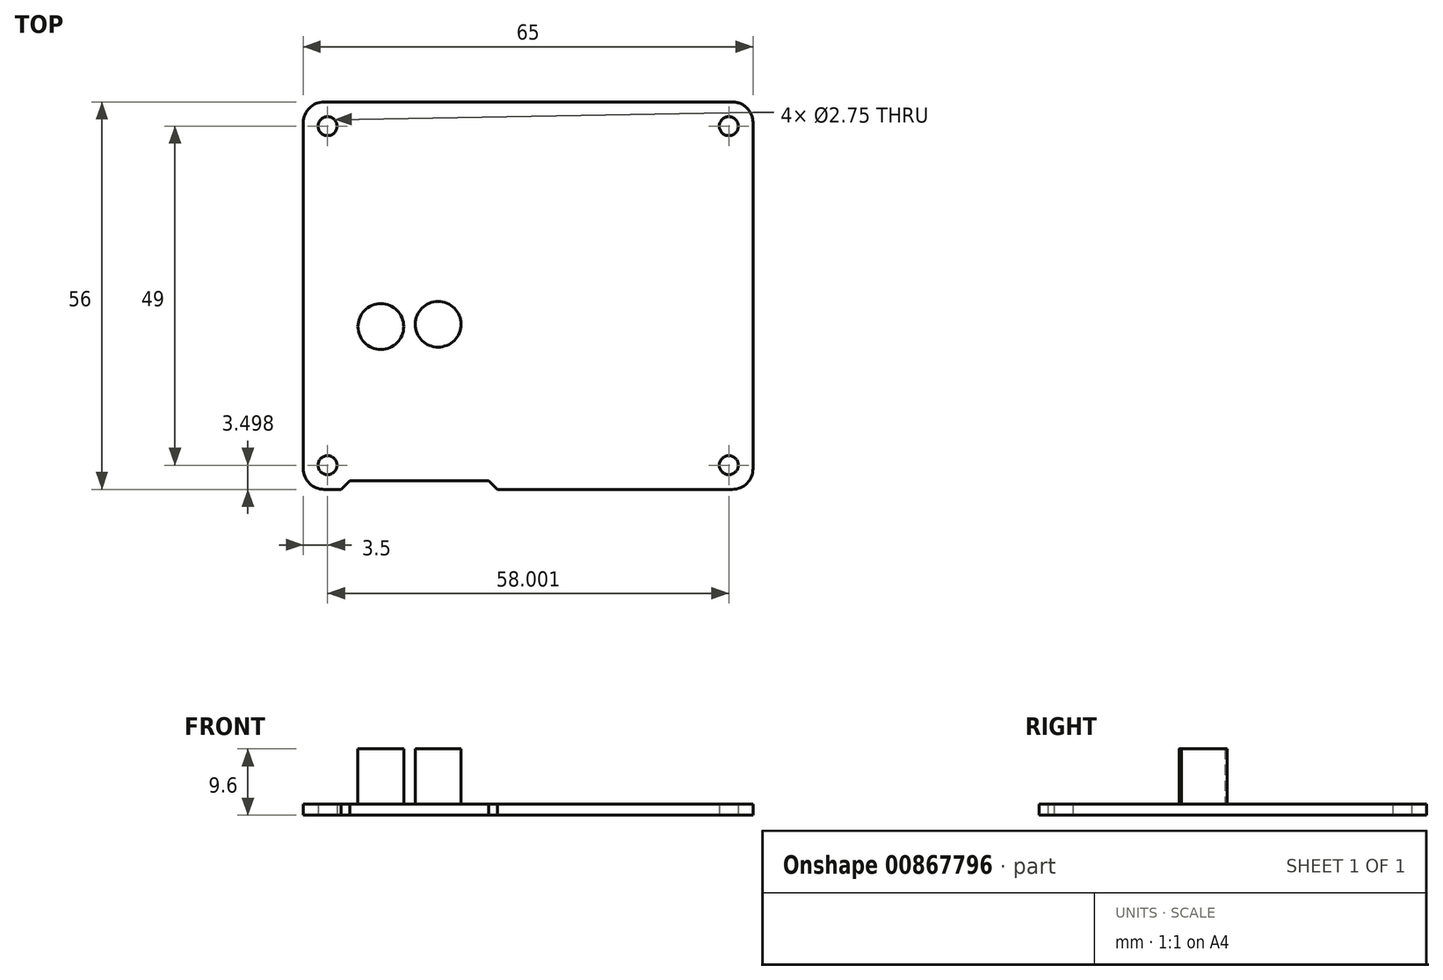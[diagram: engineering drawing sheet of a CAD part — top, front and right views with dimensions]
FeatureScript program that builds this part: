
annotation { "Feature Type Name" : "Feature", "Feature Type Description" : "" }
export const myFeature = defineFeature(function(context is Context, id is Id, definition is map)
    precondition{}
    {
        {
            var Q0;
            Q0=qCreatedBy(makeId("Top.planeOp"),FACE);
            var sketch = newSketch(context, id + "F0", { "sketchPlane" : qUnion([Q0])});
            skArc(sketch, "E0", {"start": v(-30.1, -23.27) * mm, "mid": v(-29.22, -25.4) * mm, "end": v(-27.1, -26.27) * mm});
            skArc(sketch, "E1", {"start": v(31.9, -26.27) * mm, "mid": v(34.02, -25.4) * mm, "end": v(34.9, -23.27) * mm});
            skArc(sketch, "E2", {"start": v(-27.1, 29.73) * mm, "mid": v(-29.22, 28.85) * mm, "end": v(-30.1, 26.73) * mm});
            skArc(sketch, "E3", {"start": v(34.9, 26.73) * mm, "mid": v(34.02, 28.85) * mm, "end": v(31.9, 29.73) * mm});
            skLineSegment(sketch, "E4", {"start": v(-23.37, -25) * mm, "end": v(-3.3, -25) * mm});
            skLineSegment(sketch, "E5", {"start": v(-24.64, -26.27) * mm, "end": v(-23.37, -25) * mm});
            skLineSegment(sketch, "E6", {"start": v(-2.03, -26.27) * mm, "end": v(31.9, -26.27) * mm});
            skLineSegment(sketch, "E7", {"start": v(-27.1, 29.73) * mm, "end": v(31.9, 29.73) * mm});
            skLineSegment(sketch, "E8", {"start": v(-3.3, -25) * mm, "end": v(-2.03, -26.27) * mm});
            skLineSegment(sketch, "E9", {"start": v(-30.1, -23.27) * mm, "end": v(-30.1, 26.73) * mm});
            skLineSegment(sketch, "E10", {"start": v(34.9, -23.27) * mm, "end": v(34.9, 26.73) * mm});
            skLineSegment(sketch, "E11", {"start": v(-27.97, 26.23) * mm, "end": v(-25.23, 26.23) * mm});
            skLineSegment(sketch, "E12", {"start": v(-26.6, 24.85) * mm, "end": v(-26.6, 27.6) * mm});
            skLineSegment(sketch, "E13", {"start": v(30.02, 26.23) * mm, "end": v(32.77, 26.23) * mm});
            skLineSegment(sketch, "E14", {"start": v(31.4, 24.85) * mm, "end": v(31.4, 27.6) * mm});
            skLineSegment(sketch, "E15", {"start": v(30.02, -22.77) * mm, "end": v(32.77, -22.77) * mm});
            skLineSegment(sketch, "E16", {"start": v(31.4, -24.15) * mm, "end": v(31.4, -21.4) * mm});
            skLineSegment(sketch, "E17", {"start": v(-27.97, -22.77) * mm, "end": v(-25.23, -22.77) * mm});
            skLineSegment(sketch, "E18", {"start": v(-26.6, -24.15) * mm, "end": v(-26.6, -21.4) * mm});
            skLineSegment(sketch, "E19", {"start": v(5.2, -13.06) * mm, "end": v(6.22, -13.06) * mm});
            skLineSegment(sketch, "E20", {"start": v(5.71, -13.57) * mm, "end": v(5.71, -12.56) * mm});
            skLineSegment(sketch, "E21", {"start": v(7.75, -13.06) * mm, "end": v(8.76, -13.06) * mm});
            skLineSegment(sketch, "E22", {"start": v(8.25, -13.57) * mm, "end": v(8.25, -12.56) * mm});
            skLineSegment(sketch, "E23", {"start": v(10.29, -13.06) * mm, "end": v(11.3, -13.06) * mm});
            skLineSegment(sketch, "E24", {"start": v(10.8, -13.57) * mm, "end": v(10.8, -12.56) * mm});
            skLineSegment(sketch, "E25", {"start": v(22.99, -13.06) * mm, "end": v(24, -13.06) * mm});
            skLineSegment(sketch, "E26", {"start": v(23.5, -13.57) * mm, "end": v(23.5, -12.56) * mm});
            skLineSegment(sketch, "E27", {"start": v(25.53, -13.06) * mm, "end": v(26.54, -13.06) * mm});
            skLineSegment(sketch, "E28", {"start": v(26.03, -13.57) * mm, "end": v(26.03, -12.56) * mm});
            skLineSegment(sketch, "E29", {"start": v(28.07, -13.06) * mm, "end": v(29.08, -13.06) * mm});
            skLineSegment(sketch, "E30", {"start": v(28.57, -13.57) * mm, "end": v(28.57, -12.56) * mm});
            skLineSegment(sketch, "E31", {"start": v(30.6, -13.06) * mm, "end": v(31.62, -13.06) * mm});
            skLineSegment(sketch, "E32", {"start": v(31.11, -13.57) * mm, "end": v(31.11, -12.56) * mm});
            skLineSegment(sketch, "E33", {"start": v(33.15, -13.06) * mm, "end": v(34.16, -13.06) * mm});
            skLineSegment(sketch, "E34", {"start": v(33.65, -13.57) * mm, "end": v(33.65, -12.56) * mm});
            skLineSegment(sketch, "E35", {"start": v(20.45, -13.06) * mm, "end": v(21.46, -13.06) * mm});
            skLineSegment(sketch, "E36", {"start": v(20.95, -13.57) * mm, "end": v(20.95, -12.56) * mm});
            skLineSegment(sketch, "E37", {"start": v(17.9, -13.06) * mm, "end": v(18.92, -13.06) * mm});
            skLineSegment(sketch, "E38", {"start": v(18.41, -13.57) * mm, "end": v(18.41, -12.56) * mm});
            skLineSegment(sketch, "E39", {"start": v(15.37, -13.06) * mm, "end": v(16.38, -13.06) * mm});
            skLineSegment(sketch, "E40", {"start": v(15.87, -13.57) * mm, "end": v(15.87, -12.56) * mm});
            skLineSegment(sketch, "E41", {"start": v(12.83, -13.06) * mm, "end": v(13.84, -13.06) * mm});
            skLineSegment(sketch, "E42", {"start": v(13.33, -13.57) * mm, "end": v(13.33, -12.56) * mm});
            skLineSegment(sketch, "E43", {"start": v(2.67, -13.06) * mm, "end": v(3.68, -13.06) * mm});
            skLineSegment(sketch, "E44", {"start": v(3.17, -13.57) * mm, "end": v(3.17, -12.56) * mm});
            skLineSegment(sketch, "E45", {"start": v(0.13, -13.06) * mm, "end": v(1.14, -13.06) * mm});
            skLineSegment(sketch, "E46", {"start": v(0.63, -13.57) * mm, "end": v(0.63, -12.56) * mm});
            skLineSegment(sketch, "E47", {"start": v(-2.29, -7.35) * mm, "end": v(-1.27, -7.35) * mm});
            skLineSegment(sketch, "E48", {"start": v(-1.78, -7.86) * mm, "end": v(-1.78, -6.84) * mm});
            skLineSegment(sketch, "E49", {"start": v(-2.29, -4.8) * mm, "end": v(-1.27, -4.8) * mm});
            skLineSegment(sketch, "E50", {"start": v(-1.78, -5.32) * mm, "end": v(-1.78, -4.3) * mm});
            skLineSegment(sketch, "E51", {"start": v(0.25, -7.35) * mm, "end": v(1.27, -7.35) * mm});
            skLineSegment(sketch, "E52", {"start": v(0.76, -7.86) * mm, "end": v(0.76, -6.84) * mm});
            skLineSegment(sketch, "E53", {"start": v(0.25, -4.8) * mm, "end": v(1.27, -4.8) * mm});
            skLineSegment(sketch, "E54", {"start": v(0.76, -5.32) * mm, "end": v(0.76, -4.3) * mm});
            skLineSegment(sketch, "E55", {"start": v(2.8, -7.35) * mm, "end": v(3.8, -7.35) * mm});
            skLineSegment(sketch, "E56", {"start": v(3.3, -7.86) * mm, "end": v(3.3, -6.84) * mm});
            skLineSegment(sketch, "E57", {"start": v(2.8, -4.8) * mm, "end": v(3.8, -4.8) * mm});
            skLineSegment(sketch, "E58", {"start": v(3.3, -5.32) * mm, "end": v(3.3, -4.3) * mm});
            skLineSegment(sketch, "E59", {"start": v(-15.88, 16.15) * mm, "end": v(-14.86, 16.15) * mm});
            skLineSegment(sketch, "E60", {"start": v(-15.37, 15.64) * mm, "end": v(-15.37, 16.65) * mm});
            skLineSegment(sketch, "E61", {"start": v(-18.42, 16.15) * mm, "end": v(-17.4, 16.15) * mm});
            skLineSegment(sketch, "E62", {"start": v(-17.9, 15.64) * mm, "end": v(-17.9, 16.65) * mm});
            skLineSegment(sketch, "E63", {"start": v(-18.42, 13.6) * mm, "end": v(-17.4, 13.6) * mm});
            skLineSegment(sketch, "E64", {"start": v(-17.9, 13.1) * mm, "end": v(-17.9, 14.11) * mm});
            skLineSegment(sketch, "E65", {"start": v(26.02, 27.5) * mm, "end": v(27.04, 27.5) * mm});
            skLineSegment(sketch, "E66", {"start": v(26.53, 26.99) * mm, "end": v(26.53, 28) * mm});
            skLineSegment(sketch, "E67", {"start": v(26.02, 24.96) * mm, "end": v(27.04, 24.96) * mm});
            skLineSegment(sketch, "E68", {"start": v(26.53, 24.45) * mm, "end": v(26.53, 25.46) * mm});
            skLineSegment(sketch, "E69", {"start": v(23.48, 27.5) * mm, "end": v(24.5, 27.5) * mm});
            skLineSegment(sketch, "E70", {"start": v(23.99, 26.99) * mm, "end": v(23.99, 28) * mm});
            skLineSegment(sketch, "E71", {"start": v(23.48, 24.96) * mm, "end": v(24.5, 24.96) * mm});
            skLineSegment(sketch, "E72", {"start": v(23.99, 24.45) * mm, "end": v(23.99, 25.46) * mm});
            skLineSegment(sketch, "E73", {"start": v(20.94, 27.5) * mm, "end": v(21.96, 27.5) * mm});
            skLineSegment(sketch, "E74", {"start": v(21.45, 26.99) * mm, "end": v(21.45, 28) * mm});
            skLineSegment(sketch, "E75", {"start": v(20.94, 24.96) * mm, "end": v(21.96, 24.96) * mm});
            skLineSegment(sketch, "E76", {"start": v(21.45, 24.45) * mm, "end": v(21.45, 25.46) * mm});
            skLineSegment(sketch, "E77", {"start": v(18.4, 27.5) * mm, "end": v(19.42, 27.5) * mm});
            skLineSegment(sketch, "E78", {"start": v(18.9, 26.99) * mm, "end": v(18.9, 28) * mm});
            skLineSegment(sketch, "E79", {"start": v(18.4, 24.96) * mm, "end": v(19.42, 24.96) * mm});
            skLineSegment(sketch, "E80", {"start": v(18.9, 24.45) * mm, "end": v(18.9, 25.46) * mm});
            skLineSegment(sketch, "E81", {"start": v(15.86, 27.5) * mm, "end": v(16.88, 27.5) * mm});
            skLineSegment(sketch, "E82", {"start": v(16.37, 26.99) * mm, "end": v(16.37, 28) * mm});
            skLineSegment(sketch, "E83", {"start": v(15.86, 24.96) * mm, "end": v(16.88, 24.96) * mm});
            skLineSegment(sketch, "E84", {"start": v(16.37, 24.45) * mm, "end": v(16.37, 25.46) * mm});
            skLineSegment(sketch, "E85", {"start": v(13.32, 27.5) * mm, "end": v(14.34, 27.5) * mm});
            skLineSegment(sketch, "E86", {"start": v(13.83, 26.99) * mm, "end": v(13.83, 28) * mm});
            skLineSegment(sketch, "E87", {"start": v(13.32, 24.96) * mm, "end": v(14.34, 24.96) * mm});
            skLineSegment(sketch, "E88", {"start": v(13.83, 24.45) * mm, "end": v(13.83, 25.46) * mm});
            skLineSegment(sketch, "E89", {"start": v(10.78, 27.5) * mm, "end": v(11.8, 27.5) * mm});
            skLineSegment(sketch, "E90", {"start": v(11.29, 26.99) * mm, "end": v(11.29, 28) * mm});
            skLineSegment(sketch, "E91", {"start": v(10.78, 24.96) * mm, "end": v(11.8, 24.96) * mm});
            skLineSegment(sketch, "E92", {"start": v(11.29, 24.45) * mm, "end": v(11.29, 25.46) * mm});
            skLineSegment(sketch, "E93", {"start": v(8.24, 27.5) * mm, "end": v(9.26, 27.5) * mm});
            skLineSegment(sketch, "E94", {"start": v(8.75, 26.99) * mm, "end": v(8.75, 28) * mm});
            skLineSegment(sketch, "E95", {"start": v(8.24, 24.96) * mm, "end": v(9.26, 24.96) * mm});
            skLineSegment(sketch, "E96", {"start": v(8.75, 24.45) * mm, "end": v(8.75, 25.46) * mm});
            skLineSegment(sketch, "E97", {"start": v(5.7, 27.5) * mm, "end": v(6.72, 27.5) * mm});
            skLineSegment(sketch, "E98", {"start": v(6.2, 26.99) * mm, "end": v(6.2, 28) * mm});
            skLineSegment(sketch, "E99", {"start": v(5.7, 24.96) * mm, "end": v(6.72, 24.96) * mm});
            skLineSegment(sketch, "E100", {"start": v(6.2, 24.45) * mm, "end": v(6.2, 25.46) * mm});
            skLineSegment(sketch, "E101", {"start": v(3.16, 27.5) * mm, "end": v(4.18, 27.5) * mm});
            skLineSegment(sketch, "E102", {"start": v(3.67, 26.99) * mm, "end": v(3.67, 28) * mm});
            skLineSegment(sketch, "E103", {"start": v(3.16, 24.96) * mm, "end": v(4.18, 24.96) * mm});
            skLineSegment(sketch, "E104", {"start": v(3.67, 24.45) * mm, "end": v(3.67, 25.46) * mm});
            skLineSegment(sketch, "E105", {"start": v(0.62, 27.5) * mm, "end": v(1.64, 27.5) * mm});
            skLineSegment(sketch, "E106", {"start": v(1.13, 26.99) * mm, "end": v(1.13, 28) * mm});
            skLineSegment(sketch, "E107", {"start": v(0.62, 24.96) * mm, "end": v(1.64, 24.96) * mm});
            skLineSegment(sketch, "E108", {"start": v(1.13, 24.45) * mm, "end": v(1.13, 25.46) * mm});
            skLineSegment(sketch, "E109", {"start": v(-1.92, 27.5) * mm, "end": v(-0.9, 27.5) * mm});
            skLineSegment(sketch, "E110", {"start": v(-1.41, 26.99) * mm, "end": v(-1.41, 28) * mm});
            skLineSegment(sketch, "E111", {"start": v(-1.92, 24.96) * mm, "end": v(-0.9, 24.96) * mm});
            skLineSegment(sketch, "E112", {"start": v(-1.41, 24.45) * mm, "end": v(-1.41, 25.46) * mm});
            skLineSegment(sketch, "E113", {"start": v(-4.46, 27.5) * mm, "end": v(-3.44, 27.5) * mm});
            skLineSegment(sketch, "E114", {"start": v(-3.95, 26.99) * mm, "end": v(-3.95, 28) * mm});
            skLineSegment(sketch, "E115", {"start": v(-4.46, 24.96) * mm, "end": v(-3.44, 24.96) * mm});
            skLineSegment(sketch, "E116", {"start": v(-3.95, 24.45) * mm, "end": v(-3.95, 25.46) * mm});
            skLineSegment(sketch, "E117", {"start": v(-7, 27.5) * mm, "end": v(-5.98, 27.5) * mm});
            skLineSegment(sketch, "E118", {"start": v(-6.5, 26.99) * mm, "end": v(-6.5, 28) * mm});
            skLineSegment(sketch, "E119", {"start": v(-7, 24.96) * mm, "end": v(-5.98, 24.96) * mm});
            skLineSegment(sketch, "E120", {"start": v(-6.5, 24.45) * mm, "end": v(-6.5, 25.46) * mm});
            skLineSegment(sketch, "E121", {"start": v(-9.54, 27.5) * mm, "end": v(-8.52, 27.5) * mm});
            skLineSegment(sketch, "E122", {"start": v(-9.03, 26.99) * mm, "end": v(-9.03, 28) * mm});
            skLineSegment(sketch, "E123", {"start": v(-9.54, 24.96) * mm, "end": v(-8.52, 24.96) * mm});
            skLineSegment(sketch, "E124", {"start": v(-9.03, 24.45) * mm, "end": v(-9.03, 25.46) * mm});
            skLineSegment(sketch, "E125", {"start": v(-12.08, 27.5) * mm, "end": v(-11.06, 27.5) * mm});
            skLineSegment(sketch, "E126", {"start": v(-11.57, 26.99) * mm, "end": v(-11.57, 28) * mm});
            skLineSegment(sketch, "E127", {"start": v(-12.08, 24.96) * mm, "end": v(-11.06, 24.96) * mm});
            skLineSegment(sketch, "E128", {"start": v(-11.57, 24.45) * mm, "end": v(-11.57, 25.46) * mm});
            skLineSegment(sketch, "E129", {"start": v(-14.62, 27.5) * mm, "end": v(-13.6, 27.5) * mm});
            skLineSegment(sketch, "E130", {"start": v(-14.11, 26.99) * mm, "end": v(-14.11, 28) * mm});
            skLineSegment(sketch, "E131", {"start": v(-14.62, 24.96) * mm, "end": v(-13.6, 24.96) * mm});
            skLineSegment(sketch, "E132", {"start": v(-14.11, 24.45) * mm, "end": v(-14.11, 25.46) * mm});
            skLineSegment(sketch, "E133", {"start": v(-17.16, 27.5) * mm, "end": v(-16.14, 27.5) * mm});
            skLineSegment(sketch, "E134", {"start": v(-16.65, 26.99) * mm, "end": v(-16.65, 28) * mm});
            skLineSegment(sketch, "E135", {"start": v(-17.16, 24.96) * mm, "end": v(-16.14, 24.96) * mm});
            skLineSegment(sketch, "E136", {"start": v(-16.65, 24.45) * mm, "end": v(-16.65, 25.46) * mm});
            skLineSegment(sketch, "E137", {"start": v(-19.7, 27.5) * mm, "end": v(-18.68, 27.5) * mm});
            skLineSegment(sketch, "E138", {"start": v(-19.2, 26.99) * mm, "end": v(-19.2, 28) * mm});
            skLineSegment(sketch, "E139", {"start": v(-19.7, 24.96) * mm, "end": v(-18.68, 24.96) * mm});
            skLineSegment(sketch, "E140", {"start": v(-19.2, 24.45) * mm, "end": v(-19.2, 25.46) * mm});
            skLineSegment(sketch, "E141", {"start": v(-22.24, 27.5) * mm, "end": v(-21.22, 27.5) * mm});
            skLineSegment(sketch, "E142", {"start": v(-21.73, 26.99) * mm, "end": v(-21.73, 28) * mm});
            skLineSegment(sketch, "E143", {"start": v(-22.24, 24.96) * mm, "end": v(-21.22, 24.96) * mm});
            skLineSegment(sketch, "E144", {"start": v(-21.73, 24.45) * mm, "end": v(-21.73, 25.46) * mm});
            skLineSegment(sketch, "E145", {"start": v(-8.1, -23.1) * mm, "end": v(-7.2, -23.1) * mm});
            skLineSegment(sketch, "E146", {"start": v(-7.64, -23.55) * mm, "end": v(-7.64, -22.65) * mm});
            skLineSegment(sketch, "E147", {"start": v(-11.1, -23.1) * mm, "end": v(-10.2, -23.1) * mm});
            skLineSegment(sketch, "E148", {"start": v(-10.65, -23.55) * mm, "end": v(-10.65, -22.65) * mm});
            skLineSegment(sketch, "E149", {"start": v(-7.11, -19.29) * mm, "end": v(-6.1, -19.29) * mm});
            skLineSegment(sketch, "E150", {"start": v(-6.6, -19.8) * mm, "end": v(-6.6, -18.78) * mm});
            skLineSegment(sketch, "E151", {"start": v(-9.65, -19.29) * mm, "end": v(-8.64, -19.29) * mm});
            skLineSegment(sketch, "E152", {"start": v(-9.15, -19.8) * mm, "end": v(-9.15, -18.78) * mm});
            skLineSegment(sketch, "E153", {"start": v(-12.2, -19.29) * mm, "end": v(-11.18, -19.29) * mm});
            skLineSegment(sketch, "E154", {"start": v(-11.69, -19.8) * mm, "end": v(-11.69, -18.78) * mm});
            skLineSegment(sketch, "E155", {"start": v(1.29, -24.11) * mm, "end": v(1.99, -24.11) * mm});
            skLineSegment(sketch, "E156", {"start": v(1.64, -24.46) * mm, "end": v(1.64, -23.76) * mm});
            skLineSegment(sketch, "E157", {"start": v(3.09, -24.11) * mm, "end": v(3.79, -24.11) * mm});
            skLineSegment(sketch, "E158", {"start": v(3.44, -24.46) * mm, "end": v(3.44, -23.76) * mm});
            skLineSegment(sketch, "E159", {"start": v(25.95, -24.11) * mm, "end": v(26.65, -24.11) * mm});
            skLineSegment(sketch, "E160", {"start": v(26.3, -24.46) * mm, "end": v(26.3, -23.76) * mm});
            skLineSegment(sketch, "E161", {"start": v(24.15, -24.11) * mm, "end": v(24.85, -24.11) * mm});
            skLineSegment(sketch, "E162", {"start": v(24.5, -24.46) * mm, "end": v(24.5, -23.76) * mm});
            skLineSegment(sketch, "E163", {"start": v(12.72, -24.11) * mm, "end": v(13.42, -24.11) * mm});
            skLineSegment(sketch, "E164", {"start": v(13.07, -24.46) * mm, "end": v(13.07, -23.76) * mm});
            skLineSegment(sketch, "E165", {"start": v(14.52, -24.11) * mm, "end": v(15.22, -24.11) * mm});
            skLineSegment(sketch, "E166", {"start": v(14.87, -24.46) * mm, "end": v(14.87, -23.76) * mm});
            skLineSegment(sketch, "E167", {"start": v(32.41, 15.14) * mm, "end": v(33.12, 15.14) * mm});
            skLineSegment(sketch, "E168", {"start": v(32.76, 14.8) * mm, "end": v(32.76, 15.5) * mm});
            skLineSegment(sketch, "E169", {"start": v(32.41, 13.34) * mm, "end": v(33.12, 13.34) * mm});
            skLineSegment(sketch, "E170", {"start": v(32.76, 13) * mm, "end": v(32.76, 13.69) * mm});
            skLineSegment(sketch, "E171", {"start": v(22.99, 7.26) * mm, "end": v(24, 7.26) * mm});
            skLineSegment(sketch, "E172", {"start": v(23.5, 6.75) * mm, "end": v(23.5, 7.76) * mm});
            skLineSegment(sketch, "E173", {"start": v(25.53, 7.26) * mm, "end": v(26.54, 7.26) * mm});
            skLineSegment(sketch, "E174", {"start": v(26.03, 6.75) * mm, "end": v(26.03, 7.76) * mm});
            skLineSegment(sketch, "E175", {"start": v(28.07, 7.26) * mm, "end": v(29.08, 7.26) * mm});
            skLineSegment(sketch, "E176", {"start": v(28.57, 6.75) * mm, "end": v(28.57, 7.76) * mm});
            skLineSegment(sketch, "E177", {"start": v(30.6, 7.26) * mm, "end": v(31.62, 7.26) * mm});
            skLineSegment(sketch, "E178", {"start": v(31.11, 6.75) * mm, "end": v(31.11, 7.76) * mm});
            skLineSegment(sketch, "E179", {"start": v(33.15, 7.26) * mm, "end": v(34.16, 7.26) * mm});
            skLineSegment(sketch, "E180", {"start": v(33.65, 6.75) * mm, "end": v(33.65, 7.76) * mm});
            skLineSegment(sketch, "E181", {"start": v(20.45, 7.26) * mm, "end": v(21.46, 7.26) * mm});
            skLineSegment(sketch, "E182", {"start": v(20.95, 6.75) * mm, "end": v(20.95, 7.76) * mm});
            skLineSegment(sketch, "E183", {"start": v(17.9, 7.26) * mm, "end": v(18.92, 7.26) * mm});
            skLineSegment(sketch, "E184", {"start": v(18.41, 6.75) * mm, "end": v(18.41, 7.76) * mm});
            skLineSegment(sketch, "E185", {"start": v(15.37, 7.26) * mm, "end": v(16.38, 7.26) * mm});
            skLineSegment(sketch, "E186", {"start": v(15.87, 6.75) * mm, "end": v(15.87, 7.76) * mm});
            skLineSegment(sketch, "E187", {"start": v(0.13, 4.72) * mm, "end": v(1.14, 4.72) * mm});
            skLineSegment(sketch, "E188", {"start": v(0.63, 4.2) * mm, "end": v(0.63, 5.22) * mm});
            skLineSegment(sketch, "E189", {"start": v(2.67, 4.72) * mm, "end": v(3.68, 4.72) * mm});
            skLineSegment(sketch, "E190", {"start": v(3.17, 4.2) * mm, "end": v(3.17, 5.22) * mm});
            skLineSegment(sketch, "E191", {"start": v(12.83, 4.72) * mm, "end": v(13.84, 4.72) * mm});
            skLineSegment(sketch, "E192", {"start": v(13.33, 4.2) * mm, "end": v(13.33, 5.22) * mm});
            skLineSegment(sketch, "E193", {"start": v(15.37, 4.72) * mm, "end": v(16.38, 4.72) * mm});
            skLineSegment(sketch, "E194", {"start": v(15.87, 4.2) * mm, "end": v(15.87, 5.22) * mm});
            skLineSegment(sketch, "E195", {"start": v(17.9, 4.72) * mm, "end": v(18.92, 4.72) * mm});
            skLineSegment(sketch, "E196", {"start": v(18.41, 4.2) * mm, "end": v(18.41, 5.22) * mm});
            skLineSegment(sketch, "E197", {"start": v(20.45, 4.72) * mm, "end": v(21.46, 4.72) * mm});
            skLineSegment(sketch, "E198", {"start": v(20.95, 4.2) * mm, "end": v(20.95, 5.22) * mm});
            skLineSegment(sketch, "E199", {"start": v(33.15, 4.72) * mm, "end": v(34.16, 4.72) * mm});
            skLineSegment(sketch, "E200", {"start": v(33.65, 4.2) * mm, "end": v(33.65, 5.22) * mm});
            skLineSegment(sketch, "E201", {"start": v(30.6, 4.72) * mm, "end": v(31.62, 4.72) * mm});
            skLineSegment(sketch, "E202", {"start": v(31.11, 4.2) * mm, "end": v(31.11, 5.22) * mm});
            skLineSegment(sketch, "E203", {"start": v(28.07, 4.72) * mm, "end": v(29.08, 4.72) * mm});
            skLineSegment(sketch, "E204", {"start": v(28.57, 4.2) * mm, "end": v(28.57, 5.22) * mm});
            skLineSegment(sketch, "E205", {"start": v(25.53, 4.72) * mm, "end": v(26.54, 4.72) * mm});
            skLineSegment(sketch, "E206", {"start": v(26.03, 4.2) * mm, "end": v(26.03, 5.22) * mm});
            skLineSegment(sketch, "E207", {"start": v(22.99, 4.72) * mm, "end": v(24, 4.72) * mm});
            skLineSegment(sketch, "E208", {"start": v(23.5, 4.2) * mm, "end": v(23.5, 5.22) * mm});
            skLineSegment(sketch, "E209", {"start": v(10.29, 4.72) * mm, "end": v(11.3, 4.72) * mm});
            skLineSegment(sketch, "E210", {"start": v(10.8, 4.2) * mm, "end": v(10.8, 5.22) * mm});
            skLineSegment(sketch, "E211", {"start": v(7.75, 4.72) * mm, "end": v(8.76, 4.72) * mm});
            skLineSegment(sketch, "E212", {"start": v(8.25, 4.2) * mm, "end": v(8.25, 5.22) * mm});
            skLineSegment(sketch, "E213", {"start": v(5.2, 4.72) * mm, "end": v(6.22, 4.72) * mm});
            skLineSegment(sketch, "E214", {"start": v(5.71, 4.2) * mm, "end": v(5.71, 5.22) * mm});
            skLineSegment(sketch, "E215", {"start": v(-5.59, 1.29) * mm, "end": v(-4.57, 1.29) * mm});
            skLineSegment(sketch, "E216", {"start": v(-5.08, 0.78) * mm, "end": v(-5.08, 1.8) * mm});
            skLineSegment(sketch, "E217", {"start": v(-3.05, 1.29) * mm, "end": v(-2.03, 1.29) * mm});
            skLineSegment(sketch, "E218", {"start": v(-2.54, 0.78) * mm, "end": v(-2.54, 1.8) * mm});
            skLineSegment(sketch, "E219", {"start": v(1.01, -0.87) * mm, "end": v(2.03, -0.87) * mm});
            skLineSegment(sketch, "E220", {"start": v(1.52, -1.38) * mm, "end": v(1.52, -0.36) * mm});
            skLineSegment(sketch, "E221", {"start": v(3.55, -0.87) * mm, "end": v(4.57, -0.87) * mm});
            skLineSegment(sketch, "E222", {"start": v(4.06, -1.38) * mm, "end": v(4.06, -0.36) * mm});
            skLineSegment(sketch, "E223", {"start": v(-16.95, -20.68) * mm, "end": v(-16.4, -20.68) * mm});
            skLineSegment(sketch, "E224", {"start": v(-16.68, -20.96) * mm, "end": v(-16.68, -20.41) * mm});
            skLineSegment(sketch, "E225", {"start": v(-22.95, -23.38) * mm, "end": v(-22.4, -23.38) * mm});
            skLineSegment(sketch, "E226", {"start": v(-22.68, -23.66) * mm, "end": v(-22.68, -23.11) * mm});
            skLineSegment(sketch, "E227", {"start": v(-21.95, -20.68) * mm, "end": v(-21.4, -20.68) * mm});
            skLineSegment(sketch, "E228", {"start": v(-21.68, -20.96) * mm, "end": v(-21.68, -20.41) * mm});
            skLineSegment(sketch, "E229", {"start": v(-15.95, -23.38) * mm, "end": v(-15.4, -23.38) * mm});
            skLineSegment(sketch, "E230", {"start": v(-15.68, -23.66) * mm, "end": v(-15.68, -23.11) * mm});
            skLineSegment(sketch, "E231", {"start": v(-6.41, 7.13) * mm, "end": v(-5.53, 7.13) * mm});
            skLineSegment(sketch, "E232", {"start": v(-5.97, 6.68) * mm, "end": v(-5.97, 7.57) * mm});
            skLineSegment(sketch, "E233", {"start": v(-6.41, 10.88) * mm, "end": v(-5.53, 10.88) * mm});
            skLineSegment(sketch, "E234", {"start": v(-5.97, 10.43) * mm, "end": v(-5.97, 11.32) * mm});
            skLineSegment(sketch, "E235", {"start": v(-20.14, -17.26) * mm, "end": v(-19.14, -17.26) * mm});
            skLineSegment(sketch, "E236", {"start": v(-19.64, -17.76) * mm, "end": v(-19.64, -16.76) * mm});
            skLineSegment(sketch, "E237", {"start": v(-23.14, -12.56) * mm, "end": v(-22.14, -12.56) * mm});
            skLineSegment(sketch, "E238", {"start": v(-22.64, -13.06) * mm, "end": v(-22.64, -12.06) * mm});
            skLineSegment(sketch, "E239", {"start": v(-17.14, -12.56) * mm, "end": v(-16.14, -12.56) * mm});
            skLineSegment(sketch, "E240", {"start": v(-16.64, -13.06) * mm, "end": v(-16.64, -12.06) * mm});
            skLineSegment(sketch, "E241", {"start": v(-27.05, 11.94) * mm, "end": v(-25.53, 11.94) * mm});
            skLineSegment(sketch, "E242", {"start": v(-26.3, 11.18) * mm, "end": v(-26.3, 12.7) * mm});
            skLineSegment(sketch, "E243", {"start": v(-27.05, 8.44) * mm, "end": v(-25.53, 8.44) * mm});
            skLineSegment(sketch, "E244", {"start": v(-26.3, 7.68) * mm, "end": v(-26.3, 9.2) * mm});
            skLineSegment(sketch, "E245", {"start": v(-27.05, 4.94) * mm, "end": v(-25.53, 4.94) * mm});
            skLineSegment(sketch, "E246", {"start": v(-26.3, 4.18) * mm, "end": v(-26.3, 5.7) * mm});
            skLineSegment(sketch, "E247", {"start": v(-27.05, 1.44) * mm, "end": v(-25.53, 1.44) * mm});
            skLineSegment(sketch, "E248", {"start": v(-26.3, 0.68) * mm, "end": v(-26.3, 2.2) * mm});
            skLineSegment(sketch, "E249", {"start": v(-27.05, -2.06) * mm, "end": v(-25.53, -2.06) * mm});
            skLineSegment(sketch, "E250", {"start": v(-26.3, -2.82) * mm, "end": v(-26.3, -1.3) * mm});
            skLineSegment(sketch, "E251", {"start": v(-27.05, -5.56) * mm, "end": v(-25.53, -5.56) * mm});
            skLineSegment(sketch, "E252", {"start": v(-26.3, -6.32) * mm, "end": v(-26.3, -4.8) * mm});
            skLineSegment(sketch, "E253", {"start": v(-27.05, -9.06) * mm, "end": v(-25.53, -9.06) * mm});
            skLineSegment(sketch, "E254", {"start": v(-26.3, -9.82) * mm, "end": v(-26.3, -8.3) * mm});
            skLineSegment(sketch, "E255", {"start": v(-27.05, -12.56) * mm, "end": v(-25.53, -12.56) * mm});
            skLineSegment(sketch, "E256", {"start": v(-26.3, -13.32) * mm, "end": v(-26.3, -11.8) * mm});
            skLineSegment(sketch, "E257", {"start": v(0.13, 7.26) * mm, "end": v(1.14, 7.26) * mm});
            skLineSegment(sketch, "E258", {"start": v(0.63, 6.75) * mm, "end": v(0.63, 7.76) * mm});
            skLineSegment(sketch, "E259", {"start": v(12.83, 7.26) * mm, "end": v(13.84, 7.26) * mm});
            skLineSegment(sketch, "E260", {"start": v(13.33, 6.75) * mm, "end": v(13.33, 7.76) * mm});
            skLineSegment(sketch, "E261", {"start": v(10.29, 7.26) * mm, "end": v(11.3, 7.26) * mm});
            skLineSegment(sketch, "E262", {"start": v(10.8, 6.75) * mm, "end": v(10.8, 7.76) * mm});
            skLineSegment(sketch, "E263", {"start": v(7.75, 7.26) * mm, "end": v(8.76, 7.26) * mm});
            skLineSegment(sketch, "E264", {"start": v(8.25, 6.75) * mm, "end": v(8.25, 7.76) * mm});
            skLineSegment(sketch, "E265", {"start": v(5.2, 7.26) * mm, "end": v(6.22, 7.26) * mm});
            skLineSegment(sketch, "E266", {"start": v(5.71, 6.75) * mm, "end": v(5.71, 7.76) * mm});
            skLineSegment(sketch, "E267", {"start": v(2.67, 7.26) * mm, "end": v(3.68, 7.26) * mm});
            skLineSegment(sketch, "E268", {"start": v(3.17, 6.75) * mm, "end": v(3.17, 7.76) * mm});
            skLineSegment(sketch, "E269", {"start": v(0.13, 9.8) * mm, "end": v(1.14, 9.8) * mm});
            skLineSegment(sketch, "E270", {"start": v(0.63, 9.29) * mm, "end": v(0.63, 10.3) * mm});
            skLineSegment(sketch, "E271", {"start": v(2.67, 9.8) * mm, "end": v(3.68, 9.8) * mm});
            skLineSegment(sketch, "E272", {"start": v(3.17, 9.29) * mm, "end": v(3.17, 10.3) * mm});
            skLineSegment(sketch, "E273", {"start": v(12.83, 9.8) * mm, "end": v(13.84, 9.8) * mm});
            skLineSegment(sketch, "E274", {"start": v(13.33, 9.29) * mm, "end": v(13.33, 10.3) * mm});
            skLineSegment(sketch, "E275", {"start": v(15.37, 9.8) * mm, "end": v(16.38, 9.8) * mm});
            skLineSegment(sketch, "E276", {"start": v(15.87, 9.29) * mm, "end": v(15.87, 10.3) * mm});
            skLineSegment(sketch, "E277", {"start": v(17.9, 9.8) * mm, "end": v(18.92, 9.8) * mm});
            skLineSegment(sketch, "E278", {"start": v(18.41, 9.29) * mm, "end": v(18.41, 10.3) * mm});
            skLineSegment(sketch, "E279", {"start": v(20.45, 9.8) * mm, "end": v(21.46, 9.8) * mm});
            skLineSegment(sketch, "E280", {"start": v(20.95, 9.29) * mm, "end": v(20.95, 10.3) * mm});
            skLineSegment(sketch, "E281", {"start": v(33.15, 9.8) * mm, "end": v(34.16, 9.8) * mm});
            skLineSegment(sketch, "E282", {"start": v(33.65, 9.29) * mm, "end": v(33.65, 10.3) * mm});
            skLineSegment(sketch, "E283", {"start": v(30.6, 9.8) * mm, "end": v(31.62, 9.8) * mm});
            skLineSegment(sketch, "E284", {"start": v(31.11, 9.29) * mm, "end": v(31.11, 10.3) * mm});
            skLineSegment(sketch, "E285", {"start": v(28.07, 9.8) * mm, "end": v(29.08, 9.8) * mm});
            skLineSegment(sketch, "E286", {"start": v(28.57, 9.29) * mm, "end": v(28.57, 10.3) * mm});
            skLineSegment(sketch, "E287", {"start": v(25.53, 9.8) * mm, "end": v(26.54, 9.8) * mm});
            skLineSegment(sketch, "E288", {"start": v(26.03, 9.29) * mm, "end": v(26.03, 10.3) * mm});
            skLineSegment(sketch, "E289", {"start": v(22.99, 9.8) * mm, "end": v(24, 9.8) * mm});
            skLineSegment(sketch, "E290", {"start": v(23.5, 9.29) * mm, "end": v(23.5, 10.3) * mm});
            skLineSegment(sketch, "E291", {"start": v(10.29, 9.8) * mm, "end": v(11.3, 9.8) * mm});
            skLineSegment(sketch, "E292", {"start": v(10.8, 9.29) * mm, "end": v(10.8, 10.3) * mm});
            skLineSegment(sketch, "E293", {"start": v(7.75, 9.8) * mm, "end": v(8.76, 9.8) * mm});
            skLineSegment(sketch, "E294", {"start": v(8.25, 9.29) * mm, "end": v(8.25, 10.3) * mm});
            skLineSegment(sketch, "E295", {"start": v(5.2, 9.8) * mm, "end": v(6.22, 9.8) * mm});
            skLineSegment(sketch, "E296", {"start": v(5.71, 9.29) * mm, "end": v(5.71, 10.3) * mm});
            skLineSegment(sketch, "E297", {"start": v(22.99, -15.6) * mm, "end": v(24, -15.6) * mm});
            skLineSegment(sketch, "E298", {"start": v(23.5, -16.11) * mm, "end": v(23.5, -15.1) * mm});
            skLineSegment(sketch, "E299", {"start": v(25.53, -15.6) * mm, "end": v(26.54, -15.6) * mm});
            skLineSegment(sketch, "E300", {"start": v(26.03, -16.11) * mm, "end": v(26.03, -15.1) * mm});
            skLineSegment(sketch, "E301", {"start": v(28.07, -15.6) * mm, "end": v(29.08, -15.6) * mm});
            skLineSegment(sketch, "E302", {"start": v(28.57, -16.11) * mm, "end": v(28.57, -15.1) * mm});
            skLineSegment(sketch, "E303", {"start": v(30.6, -15.6) * mm, "end": v(31.62, -15.6) * mm});
            skLineSegment(sketch, "E304", {"start": v(31.11, -16.11) * mm, "end": v(31.11, -15.1) * mm});
            skLineSegment(sketch, "E305", {"start": v(33.15, -15.6) * mm, "end": v(34.16, -15.6) * mm});
            skLineSegment(sketch, "E306", {"start": v(33.65, -16.11) * mm, "end": v(33.65, -15.1) * mm});
            skLineSegment(sketch, "E307", {"start": v(20.45, -15.6) * mm, "end": v(21.46, -15.6) * mm});
            skLineSegment(sketch, "E308", {"start": v(20.95, -16.11) * mm, "end": v(20.95, -15.1) * mm});
            skLineSegment(sketch, "E309", {"start": v(0.13, -15.6) * mm, "end": v(1.14, -15.6) * mm});
            skLineSegment(sketch, "E310", {"start": v(0.63, -16.11) * mm, "end": v(0.63, -15.1) * mm});
            skLineSegment(sketch, "E311", {"start": v(2.67, -15.6) * mm, "end": v(3.68, -15.6) * mm});
            skLineSegment(sketch, "E312", {"start": v(3.17, -16.11) * mm, "end": v(3.17, -15.1) * mm});
            skLineSegment(sketch, "E313", {"start": v(5.2, -15.6) * mm, "end": v(6.22, -15.6) * mm});
            skLineSegment(sketch, "E314", {"start": v(5.71, -16.11) * mm, "end": v(5.71, -15.1) * mm});
            skLineSegment(sketch, "E315", {"start": v(17.9, -15.6) * mm, "end": v(18.92, -15.6) * mm});
            skLineSegment(sketch, "E316", {"start": v(18.41, -16.11) * mm, "end": v(18.41, -15.1) * mm});
            skLineSegment(sketch, "E317", {"start": v(15.37, -15.6) * mm, "end": v(16.38, -15.6) * mm});
            skLineSegment(sketch, "E318", {"start": v(15.87, -16.11) * mm, "end": v(15.87, -15.1) * mm});
            skLineSegment(sketch, "E319", {"start": v(12.83, -15.6) * mm, "end": v(13.84, -15.6) * mm});
            skLineSegment(sketch, "E320", {"start": v(13.33, -16.11) * mm, "end": v(13.33, -15.1) * mm});
            skLineSegment(sketch, "E321", {"start": v(10.29, -15.6) * mm, "end": v(11.3, -15.6) * mm});
            skLineSegment(sketch, "E322", {"start": v(10.8, -16.11) * mm, "end": v(10.8, -15.1) * mm});
            skLineSegment(sketch, "E323", {"start": v(7.75, -15.6) * mm, "end": v(8.76, -15.6) * mm});
            skLineSegment(sketch, "E324", {"start": v(8.25, -16.11) * mm, "end": v(8.25, -15.1) * mm});
            skLineSegment(sketch, "E325", {"start": v(0.13, -18.14) * mm, "end": v(1.14, -18.14) * mm});
            skLineSegment(sketch, "E326", {"start": v(0.63, -18.65) * mm, "end": v(0.63, -17.64) * mm});
            skLineSegment(sketch, "E327", {"start": v(2.67, -18.14) * mm, "end": v(3.68, -18.14) * mm});
            skLineSegment(sketch, "E328", {"start": v(3.17, -18.65) * mm, "end": v(3.17, -17.64) * mm});
            skLineSegment(sketch, "E329", {"start": v(12.83, -18.14) * mm, "end": v(13.84, -18.14) * mm});
            skLineSegment(sketch, "E330", {"start": v(13.33, -18.65) * mm, "end": v(13.33, -17.64) * mm});
            skLineSegment(sketch, "E331", {"start": v(15.37, -18.14) * mm, "end": v(16.38, -18.14) * mm});
            skLineSegment(sketch, "E332", {"start": v(15.87, -18.65) * mm, "end": v(15.87, -17.64) * mm});
            skLineSegment(sketch, "E333", {"start": v(17.9, -18.14) * mm, "end": v(18.92, -18.14) * mm});
            skLineSegment(sketch, "E334", {"start": v(18.41, -18.65) * mm, "end": v(18.41, -17.64) * mm});
            skLineSegment(sketch, "E335", {"start": v(20.45, -18.14) * mm, "end": v(21.46, -18.14) * mm});
            skLineSegment(sketch, "E336", {"start": v(20.95, -18.65) * mm, "end": v(20.95, -17.64) * mm});
            skLineSegment(sketch, "E337", {"start": v(33.15, -18.14) * mm, "end": v(34.16, -18.14) * mm});
            skLineSegment(sketch, "E338", {"start": v(33.65, -18.65) * mm, "end": v(33.65, -17.64) * mm});
            skLineSegment(sketch, "E339", {"start": v(30.6, -18.14) * mm, "end": v(31.62, -18.14) * mm});
            skLineSegment(sketch, "E340", {"start": v(31.11, -18.65) * mm, "end": v(31.11, -17.64) * mm});
            skLineSegment(sketch, "E341", {"start": v(28.07, -18.14) * mm, "end": v(29.08, -18.14) * mm});
            skLineSegment(sketch, "E342", {"start": v(28.57, -18.65) * mm, "end": v(28.57, -17.64) * mm});
            skLineSegment(sketch, "E343", {"start": v(25.53, -18.14) * mm, "end": v(26.54, -18.14) * mm});
            skLineSegment(sketch, "E344", {"start": v(26.03, -18.65) * mm, "end": v(26.03, -17.64) * mm});
            skLineSegment(sketch, "E345", {"start": v(22.99, -18.14) * mm, "end": v(24, -18.14) * mm});
            skLineSegment(sketch, "E346", {"start": v(23.5, -18.65) * mm, "end": v(23.5, -17.64) * mm});
            skLineSegment(sketch, "E347", {"start": v(10.29, -18.14) * mm, "end": v(11.3, -18.14) * mm});
            skLineSegment(sketch, "E348", {"start": v(10.8, -18.65) * mm, "end": v(10.8, -17.64) * mm});
            skLineSegment(sketch, "E349", {"start": v(7.75, -18.14) * mm, "end": v(8.76, -18.14) * mm});
            skLineSegment(sketch, "E350", {"start": v(8.25, -18.65) * mm, "end": v(8.25, -17.64) * mm});
            skLineSegment(sketch, "E351", {"start": v(5.2, -18.14) * mm, "end": v(6.22, -18.14) * mm});
            skLineSegment(sketch, "E352", {"start": v(5.71, -18.65) * mm, "end": v(5.71, -17.64) * mm});
            skLineSegment(sketch, "E353", {"start": v(22.22, 21.23) * mm, "end": v(23.24, 21.23) * mm});
            skLineSegment(sketch, "E354", {"start": v(22.73, 20.72) * mm, "end": v(22.73, 21.73) * mm});
            skLineSegment(sketch, "E355", {"start": v(24.76, 21.23) * mm, "end": v(25.78, 21.23) * mm});
            skLineSegment(sketch, "E356", {"start": v(25.27, 20.72) * mm, "end": v(25.27, 21.73) * mm});
            skLineSegment(sketch, "E357", {"start": v(27.3, 21.23) * mm, "end": v(28.32, 21.23) * mm});
            skLineSegment(sketch, "E358", {"start": v(27.81, 20.72) * mm, "end": v(27.81, 21.73) * mm});
            skLineSegment(sketch, "E359", {"start": v(29.84, 21.23) * mm, "end": v(30.86, 21.23) * mm});
            skLineSegment(sketch, "E360", {"start": v(30.35, 20.72) * mm, "end": v(30.35, 21.73) * mm});
            skLineSegment(sketch, "E361", {"start": v(32.38, 21.23) * mm, "end": v(33.4, 21.23) * mm});
            skLineSegment(sketch, "E362", {"start": v(32.9, 20.72) * mm, "end": v(32.9, 21.73) * mm});
            skLineSegment(sketch, "E363", {"start": v(19.68, 21.23) * mm, "end": v(20.7, 21.23) * mm});
            skLineSegment(sketch, "E364", {"start": v(20.2, 20.72) * mm, "end": v(20.2, 21.73) * mm});
            skLineSegment(sketch, "E365", {"start": v(17.14, 21.23) * mm, "end": v(18.16, 21.23) * mm});
            skLineSegment(sketch, "E366", {"start": v(17.65, 20.72) * mm, "end": v(17.65, 21.73) * mm});
            skLineSegment(sketch, "E367", {"start": v(14.6, 21.23) * mm, "end": v(15.62, 21.23) * mm});
            skLineSegment(sketch, "E368", {"start": v(15.11, 20.72) * mm, "end": v(15.11, 21.73) * mm});
            skLineSegment(sketch, "E369", {"start": v(12.06, 21.23) * mm, "end": v(13.08, 21.23) * mm});
            skLineSegment(sketch, "E370", {"start": v(12.57, 20.72) * mm, "end": v(12.57, 21.73) * mm});
            skLineSegment(sketch, "E371", {"start": v(9.52, 21.23) * mm, "end": v(10.54, 21.23) * mm});
            skLineSegment(sketch, "E372", {"start": v(10.03, 20.72) * mm, "end": v(10.03, 21.73) * mm});
            skLineSegment(sketch, "E373", {"start": v(6.98, 21.23) * mm, "end": v(8, 21.23) * mm});
            skLineSegment(sketch, "E374", {"start": v(7.5, 20.72) * mm, "end": v(7.5, 21.73) * mm});
            skLineSegment(sketch, "E375", {"start": v(4.44, 21.23) * mm, "end": v(5.46, 21.23) * mm});
            skLineSegment(sketch, "E376", {"start": v(4.95, 20.72) * mm, "end": v(4.95, 21.73) * mm});
            skLineSegment(sketch, "E377", {"start": v(1.9, 21.23) * mm, "end": v(2.92, 21.23) * mm});
            skLineSegment(sketch, "E378", {"start": v(2.41, 20.72) * mm, "end": v(2.41, 21.73) * mm});
            skLineSegment(sketch, "E379", {"start": v(-8.26, 21.23) * mm, "end": v(-7.24, 21.23) * mm});
            skLineSegment(sketch, "E380", {"start": v(-7.75, 20.72) * mm, "end": v(-7.75, 21.73) * mm});
            skLineSegment(sketch, "E381", {"start": v(-10.8, 21.23) * mm, "end": v(-9.78, 21.23) * mm});
            skLineSegment(sketch, "E382", {"start": v(-10.29, 20.72) * mm, "end": v(-10.29, 21.73) * mm});
            skLineSegment(sketch, "E383", {"start": v(-13.34, 21.23) * mm, "end": v(-12.32, 21.23) * mm});
            skLineSegment(sketch, "E384", {"start": v(-12.83, 20.72) * mm, "end": v(-12.83, 21.73) * mm});
            skLineSegment(sketch, "E385", {"start": v(-15.88, 21.23) * mm, "end": v(-14.86, 21.23) * mm});
            skLineSegment(sketch, "E386", {"start": v(-15.37, 20.72) * mm, "end": v(-15.37, 21.73) * mm});
            skLineSegment(sketch, "E387", {"start": v(-28.58, 21.23) * mm, "end": v(-27.56, 21.23) * mm});
            skLineSegment(sketch, "E388", {"start": v(-28.07, 20.72) * mm, "end": v(-28.07, 21.73) * mm});
            skLineSegment(sketch, "E389", {"start": v(-26.04, 21.23) * mm, "end": v(-25.02, 21.23) * mm});
            skLineSegment(sketch, "E390", {"start": v(-25.53, 20.72) * mm, "end": v(-25.53, 21.73) * mm});
            skLineSegment(sketch, "E391", {"start": v(-23.5, 21.23) * mm, "end": v(-22.48, 21.23) * mm});
            skLineSegment(sketch, "E392", {"start": v(-22.99, 20.72) * mm, "end": v(-22.99, 21.73) * mm});
            skLineSegment(sketch, "E393", {"start": v(-20.96, 21.23) * mm, "end": v(-19.94, 21.23) * mm});
            skLineSegment(sketch, "E394", {"start": v(-20.45, 20.72) * mm, "end": v(-20.45, 21.73) * mm});
            skLineSegment(sketch, "E395", {"start": v(-18.42, 21.23) * mm, "end": v(-17.4, 21.23) * mm});
            skLineSegment(sketch, "E396", {"start": v(-17.9, 20.72) * mm, "end": v(-17.9, 21.73) * mm});
            skLineSegment(sketch, "E397", {"start": v(-5.72, 21.23) * mm, "end": v(-4.7, 21.23) * mm});
            skLineSegment(sketch, "E398", {"start": v(-5.2, 20.72) * mm, "end": v(-5.2, 21.73) * mm});
            skLineSegment(sketch, "E399", {"start": v(-3.18, 21.23) * mm, "end": v(-2.16, 21.23) * mm});
            skLineSegment(sketch, "E400", {"start": v(-2.67, 20.72) * mm, "end": v(-2.67, 21.73) * mm});
            skLineSegment(sketch, "E401", {"start": v(-0.64, 21.23) * mm, "end": v(0.38, 21.23) * mm});
            skLineSegment(sketch, "E402", {"start": v(-0.13, 20.72) * mm, "end": v(-0.13, 21.73) * mm});
            skLineSegment(sketch, "E403", {"start": v(32.38, 18.69) * mm, "end": v(33.4, 18.69) * mm});
            skLineSegment(sketch, "E404", {"start": v(32.9, 18.18) * mm, "end": v(32.9, 19.2) * mm});
            skLineSegment(sketch, "E405", {"start": v(7.11, 16.15) * mm, "end": v(8.13, 16.15) * mm});
            skLineSegment(sketch, "E406", {"start": v(7.62, 15.64) * mm, "end": v(7.62, 16.65) * mm});
            skLineSegment(sketch, "E407", {"start": v(22.35, 13.6) * mm, "end": v(23.37, 13.6) * mm});
            skLineSegment(sketch, "E408", {"start": v(22.86, 13.1) * mm, "end": v(22.86, 14.11) * mm});
            skLineSegment(sketch, "E409", {"start": v(27.43, 16.15) * mm, "end": v(28.45, 16.15) * mm});
            skLineSegment(sketch, "E410", {"start": v(27.94, 15.64) * mm, "end": v(27.94, 16.65) * mm});
            skLineSegment(sketch, "E411", {"start": v(22.35, 16.15) * mm, "end": v(23.37, 16.15) * mm});
            skLineSegment(sketch, "E412", {"start": v(22.86, 15.64) * mm, "end": v(22.86, 16.65) * mm});
            skLineSegment(sketch, "E413", {"start": v(12.2, 16.15) * mm, "end": v(13.2, 16.15) * mm});
            skLineSegment(sketch, "E414", {"start": v(12.7, 15.64) * mm, "end": v(12.7, 16.65) * mm});
            skLineSegment(sketch, "E415", {"start": v(27.43, 13.6) * mm, "end": v(28.45, 13.6) * mm});
            skLineSegment(sketch, "E416", {"start": v(27.94, 13.1) * mm, "end": v(27.94, 14.11) * mm});
            skLineSegment(sketch, "E417", {"start": v(7.11, 13.6) * mm, "end": v(8.13, 13.6) * mm});
            skLineSegment(sketch, "E418", {"start": v(7.62, 13.1) * mm, "end": v(7.62, 14.11) * mm});
            skLineSegment(sketch, "E419", {"start": v(14.73, 13.6) * mm, "end": v(15.75, 13.6) * mm});
            skLineSegment(sketch, "E420", {"start": v(15.24, 13.1) * mm, "end": v(15.24, 14.11) * mm});
            skLineSegment(sketch, "E421", {"start": v(19.81, 16.15) * mm, "end": v(20.83, 16.15) * mm});
            skLineSegment(sketch, "E422", {"start": v(20.32, 15.64) * mm, "end": v(20.32, 16.65) * mm});
            skLineSegment(sketch, "E423", {"start": v(14.73, 16.15) * mm, "end": v(15.75, 16.15) * mm});
            skLineSegment(sketch, "E424", {"start": v(15.24, 15.64) * mm, "end": v(15.24, 16.65) * mm});
            skLineSegment(sketch, "E425", {"start": v(12.2, 13.6) * mm, "end": v(13.2, 13.6) * mm});
            skLineSegment(sketch, "E426", {"start": v(12.7, 13.1) * mm, "end": v(12.7, 14.11) * mm});
            skLineSegment(sketch, "E427", {"start": v(19.81, 13.6) * mm, "end": v(20.83, 13.6) * mm});
            skLineSegment(sketch, "E428", {"start": v(20.32, 13.1) * mm, "end": v(20.32, 14.11) * mm});
            skLineSegment(sketch, "E429", {"start": v(-15.88, 13.6) * mm, "end": v(-14.86, 13.6) * mm});
            skLineSegment(sketch, "E430", {"start": v(-15.37, 13.1) * mm, "end": v(-15.37, 14.11) * mm});
            skLineSegment(sketch, "E431", {"start": v(-13.34, 13.6) * mm, "end": v(-12.32, 13.6) * mm});
            skLineSegment(sketch, "E432", {"start": v(-12.83, 13.1) * mm, "end": v(-12.83, 14.11) * mm});
            skLineSegment(sketch, "E433", {"start": v(-29.34, -3.16) * mm, "end": v(-28.32, -3.16) * mm});
            skLineSegment(sketch, "E434", {"start": v(-28.83, -3.67) * mm, "end": v(-28.83, -2.65) * mm});
            skLineSegment(sketch, "E435", {"start": v(-29.34, 9.54) * mm, "end": v(-28.32, 9.54) * mm});
            skLineSegment(sketch, "E436", {"start": v(-28.83, 9.03) * mm, "end": v(-28.83, 10.05) * mm});
            skLineSegment(sketch, "E437", {"start": v(-29.34, 7) * mm, "end": v(-28.32, 7) * mm});
            skLineSegment(sketch, "E438", {"start": v(-28.83, 6.5) * mm, "end": v(-28.83, 7.5) * mm});
            skLineSegment(sketch, "E439", {"start": v(-29.34, 4.46) * mm, "end": v(-28.32, 4.46) * mm});
            skLineSegment(sketch, "E440", {"start": v(-28.83, 3.95) * mm, "end": v(-28.83, 4.97) * mm});
            skLineSegment(sketch, "E441", {"start": v(-29.34, 1.92) * mm, "end": v(-28.32, 1.92) * mm});
            skLineSegment(sketch, "E442", {"start": v(-28.83, 1.41) * mm, "end": v(-28.83, 2.43) * mm});
            skLineSegment(sketch, "E443", {"start": v(-29.34, -0.62) * mm, "end": v(-28.32, -0.62) * mm});
            skLineSegment(sketch, "E444", {"start": v(-28.83, -1.13) * mm, "end": v(-28.83, -0.11) * mm});
            skLineSegment(sketch, "E445", {"start": v(-29.34, -9.54) * mm, "end": v(-28.32, -9.54) * mm});
            skLineSegment(sketch, "E446", {"start": v(-28.83, -10.05) * mm, "end": v(-28.83, -9.03) * mm});
            skLineSegment(sketch, "E447", {"start": v(-29.34, -12.08) * mm, "end": v(-28.32, -12.08) * mm});
            skLineSegment(sketch, "E448", {"start": v(-28.83, -12.59) * mm, "end": v(-28.83, -11.57) * mm});
            skLineSegment(sketch, "E449", {"start": v(-14.35, -14.33) * mm, "end": v(-13.34, -14.33) * mm});
            skLineSegment(sketch, "E450", {"start": v(-13.84, -14.84) * mm, "end": v(-13.84, -13.83) * mm});
            skLineSegment(sketch, "E451", {"start": v(-11.81, -14.33) * mm, "end": v(-10.8, -14.33) * mm});
            skLineSegment(sketch, "E452", {"start": v(-11.3, -14.84) * mm, "end": v(-11.3, -13.83) * mm});
            skLineSegment(sketch, "E453", {"start": v(33.15, -6.71) * mm, "end": v(34.16, -6.71) * mm});
            skLineSegment(sketch, "E454", {"start": v(33.65, -7.22) * mm, "end": v(33.65, -6.2) * mm});
            skLineSegment(sketch, "E455", {"start": v(30.6, -6.71) * mm, "end": v(31.62, -6.71) * mm});
            skLineSegment(sketch, "E456", {"start": v(31.11, -7.22) * mm, "end": v(31.11, -6.2) * mm});
            skLineSegment(sketch, "E457", {"start": v(33.15, -4.17) * mm, "end": v(34.16, -4.17) * mm});
            skLineSegment(sketch, "E458", {"start": v(33.65, -4.68) * mm, "end": v(33.65, -3.67) * mm});
            skLineSegment(sketch, "E459", {"start": v(30.6, -1.63) * mm, "end": v(31.62, -1.63) * mm});
            skLineSegment(sketch, "E460", {"start": v(31.11, -2.14) * mm, "end": v(31.11, -1.13) * mm});
            skLineSegment(sketch, "E461", {"start": v(33.15, -1.63) * mm, "end": v(34.16, -1.63) * mm});
            skLineSegment(sketch, "E462", {"start": v(33.65, -2.14) * mm, "end": v(33.65, -1.13) * mm});
            skLineSegment(sketch, "E463", {"start": v(30.6, -4.17) * mm, "end": v(31.62, -4.17) * mm});
            skLineSegment(sketch, "E464", {"start": v(31.11, -4.68) * mm, "end": v(31.11, -3.67) * mm});
            skLineSegment(sketch, "E465", {"start": v(-13.34, 16.15) * mm, "end": v(-12.32, 16.15) * mm});
            skLineSegment(sketch, "E466", {"start": v(-12.83, 15.64) * mm, "end": v(-12.83, 16.65) * mm});
            skLineSegment(sketch, "E467", {"start": v(31.56, 14.24) * mm, "end": v(31.94, 14.24) * mm});
            skLineSegment(sketch, "E468", {"start": v(31.75, 14.05) * mm, "end": v(31.75, 14.43) * mm});
            skLineSegment(sketch, "E469", {"start": v(25.08, 18.69) * mm, "end": v(25.46, 18.69) * mm});
            skLineSegment(sketch, "E470", {"start": v(25.27, 18.5) * mm, "end": v(25.27, 18.88) * mm});
            skLineSegment(sketch, "E471", {"start": v(21.27, 18.69) * mm, "end": v(21.65, 18.69) * mm});
            skLineSegment(sketch, "E472", {"start": v(21.46, 18.5) * mm, "end": v(21.46, 18.88) * mm});
            skLineSegment(sketch, "E473", {"start": v(17.46, 18.69) * mm, "end": v(17.84, 18.69) * mm});
            skLineSegment(sketch, "E474", {"start": v(17.65, 18.5) * mm, "end": v(17.65, 18.88) * mm});
            skLineSegment(sketch, "E475", {"start": v(-11.88, 4.2) * mm, "end": v(-11.5, 4.2) * mm});
            skLineSegment(sketch, "E476", {"start": v(-11.69, 4.02) * mm, "end": v(-11.69, 4.4) * mm});
            skLineSegment(sketch, "E477", {"start": v(-10.6, 2.56) * mm, "end": v(-10.22, 2.56) * mm});
            skLineSegment(sketch, "E478", {"start": v(-10.42, 2.37) * mm, "end": v(-10.42, 2.75) * mm});
            skLineSegment(sketch, "E479", {"start": v(-10.6, 1.8) * mm, "end": v(-10.22, 1.8) * mm});
            skLineSegment(sketch, "E480", {"start": v(-10.42, 1.6) * mm, "end": v(-10.42, 1.99) * mm});
            skLineSegment(sketch, "E481", {"start": v(-16.07, 5.35) * mm, "end": v(-15.69, 5.35) * mm});
            skLineSegment(sketch, "E482", {"start": v(-15.88, 5.16) * mm, "end": v(-15.88, 5.54) * mm});
            skLineSegment(sketch, "E483", {"start": v(-16.32, 4.59) * mm, "end": v(-15.94, 4.59) * mm});
            skLineSegment(sketch, "E484", {"start": v(-16.13, 4.4) * mm, "end": v(-16.13, 4.78) * mm});
            skLineSegment(sketch, "E485", {"start": v(-21.65, 0.52) * mm, "end": v(-21.27, 0.52) * mm});
            skLineSegment(sketch, "E486", {"start": v(-21.46, 0.33) * mm, "end": v(-21.46, 0.72) * mm});
            skLineSegment(sketch, "E487", {"start": v(-20.9, 0.65) * mm, "end": v(-20.51, 0.65) * mm});
            skLineSegment(sketch, "E488", {"start": v(-20.7, 0.46) * mm, "end": v(-20.7, 0.84) * mm});
            skLineSegment(sketch, "E489", {"start": v(-20.9, 1.41) * mm, "end": v(-20.51, 1.41) * mm});
            skLineSegment(sketch, "E490", {"start": v(-20.7, 1.22) * mm, "end": v(-20.7, 1.6) * mm});
            skLineSegment(sketch, "E491", {"start": v(-18.1, 8.65) * mm, "end": v(-17.72, 8.65) * mm});
            skLineSegment(sketch, "E492", {"start": v(-17.9, 8.46) * mm, "end": v(-17.9, 8.84) * mm});
            skLineSegment(sketch, "E493", {"start": v(-18.86, 8.9) * mm, "end": v(-18.48, 8.9) * mm});
            skLineSegment(sketch, "E494", {"start": v(-18.67, 8.72) * mm, "end": v(-18.67, 9.1) * mm});
            skLineSegment(sketch, "E495", {"start": v(-18.54, 10.05) * mm, "end": v(-18.04, 10.05) * mm});
            skLineSegment(sketch, "E496", {"start": v(-18.29, 9.8) * mm, "end": v(-18.29, 10.3) * mm});
            skLineSegment(sketch, "E497", {"start": v(-18.54, 5.73) * mm, "end": v(-18.04, 5.73) * mm});
            skLineSegment(sketch, "E498", {"start": v(-18.29, 5.48) * mm, "end": v(-18.29, 5.99) * mm});
            skLineSegment(sketch, "E499", {"start": v(-21.9, 12.97) * mm, "end": v(-21.53, 12.97) * mm});
            skLineSegment(sketch, "E500", {"start": v(-21.72, 12.78) * mm, "end": v(-21.72, 13.16) * mm});
            skLineSegment(sketch, "E501", {"start": v(-21.27, 12.59) * mm, "end": v(-20.9, 12.59) * mm});
            skLineSegment(sketch, "E502", {"start": v(-21.08, 12.4) * mm, "end": v(-21.08, 12.78) * mm});
            skLineSegment(sketch, "E503", {"start": v(-20.82, 11.95) * mm, "end": v(-20.44, 11.95) * mm});
            skLineSegment(sketch, "E504", {"start": v(-20.63, 11.76) * mm, "end": v(-20.63, 12.15) * mm});
            skLineSegment(sketch, "E505", {"start": v(-6.03, -2.78) * mm, "end": v(-5.65, -2.78) * mm});
            skLineSegment(sketch, "E506", {"start": v(-5.84, -2.97) * mm, "end": v(-5.84, -2.59) * mm});
            skLineSegment(sketch, "E507", {"start": v(-6.03, -3.54) * mm, "end": v(-5.65, -3.54) * mm});
            skLineSegment(sketch, "E508", {"start": v(-5.84, -3.73) * mm, "end": v(-5.84, -3.35) * mm});
            skLineSegment(sketch, "E509", {"start": v(-8.83, -4.68) * mm, "end": v(-8.45, -4.68) * mm});
            skLineSegment(sketch, "E510", {"start": v(-8.64, -4.87) * mm, "end": v(-8.64, -4.5) * mm});
            skLineSegment(sketch, "E511", {"start": v(-8.83, -3.92) * mm, "end": v(-8.45, -3.92) * mm});
            skLineSegment(sketch, "E512", {"start": v(-8.64, -4.11) * mm, "end": v(-8.64, -3.73) * mm});
            skLineSegment(sketch, "E513", {"start": v(-3.75, -4.56) * mm, "end": v(-3.37, -4.56) * mm});
            skLineSegment(sketch, "E514", {"start": v(-3.56, -4.75) * mm, "end": v(-3.56, -4.36) * mm});
            skLineSegment(sketch, "E515", {"start": v(-3.75, -5.32) * mm, "end": v(-3.37, -5.32) * mm});
            skLineSegment(sketch, "E516", {"start": v(-3.56, -5.5) * mm, "end": v(-3.56, -5.13) * mm});
            skLineSegment(sketch, "E517", {"start": v(-3.75, -6.08) * mm, "end": v(-3.37, -6.08) * mm});
            skLineSegment(sketch, "E518", {"start": v(-3.56, -6.27) * mm, "end": v(-3.56, -5.89) * mm});
            skLineSegment(sketch, "E519", {"start": v(-3.75, -6.84) * mm, "end": v(-3.37, -6.84) * mm});
            skLineSegment(sketch, "E520", {"start": v(-3.56, -7.03) * mm, "end": v(-3.56, -6.65) * mm});
            skLineSegment(sketch, "E521", {"start": v(-8.57, 4.08) * mm, "end": v(-8.2, 4.08) * mm});
            skLineSegment(sketch, "E522", {"start": v(-8.38, 3.9) * mm, "end": v(-8.38, 4.27) * mm});
            skLineSegment(sketch, "E523", {"start": v(-19.37, 6.5) * mm, "end": v(-18.99, 6.5) * mm});
            skLineSegment(sketch, "E524", {"start": v(-19.18, 6.3) * mm, "end": v(-19.18, 6.68) * mm});
            skLineSegment(sketch, "E525", {"start": v(-20.13, 6.5) * mm, "end": v(-19.75, 6.5) * mm});
            skLineSegment(sketch, "E526", {"start": v(-19.94, 6.3) * mm, "end": v(-19.94, 6.68) * mm});
            skLineSegment(sketch, "E527", {"start": v(-20.77, 7) * mm, "end": v(-20.38, 7) * mm});
            skLineSegment(sketch, "E528", {"start": v(-20.58, 6.81) * mm, "end": v(-20.58, 7.2) * mm});
            skLineSegment(sketch, "E529", {"start": v(-12.64, -12.81) * mm, "end": v(-12.26, -12.81) * mm});
            skLineSegment(sketch, "E530", {"start": v(-12.45, -13) * mm, "end": v(-12.45, -12.62) * mm});
            skLineSegment(sketch, "E531", {"start": v(-10.66, -5.7) * mm, "end": v(-10.28, -5.7) * mm});
            skLineSegment(sketch, "E532", {"start": v(-10.47, -5.89) * mm, "end": v(-10.47, -5.5) * mm});
            skLineSegment(sketch, "E533", {"start": v(-10.99, -10.65) * mm, "end": v(-10.6, -10.65) * mm});
            skLineSegment(sketch, "E534", {"start": v(-10.8, -10.84) * mm, "end": v(-10.8, -10.46) * mm});
            skLineSegment(sketch, "E535", {"start": v(-11.75, -10.65) * mm, "end": v(-11.37, -10.65) * mm});
            skLineSegment(sketch, "E536", {"start": v(-11.56, -10.84) * mm, "end": v(-11.56, -10.46) * mm});
            skLineSegment(sketch, "E537", {"start": v(-12.51, -10.65) * mm, "end": v(-12.13, -10.65) * mm});
            skLineSegment(sketch, "E538", {"start": v(-12.32, -10.84) * mm, "end": v(-12.32, -10.46) * mm});
            skLineSegment(sketch, "E539", {"start": v(-10.99, -11.41) * mm, "end": v(-10.6, -11.41) * mm});
            skLineSegment(sketch, "E540", {"start": v(-10.8, -11.6) * mm, "end": v(-10.8, -11.22) * mm});
            skLineSegment(sketch, "E541", {"start": v(-12.9, -10.02) * mm, "end": v(-12.51, -10.02) * mm});
            skLineSegment(sketch, "E542", {"start": v(-12.7, -10.2) * mm, "end": v(-12.7, -9.83) * mm});
            skLineSegment(sketch, "E543", {"start": v(-11.75, -11.41) * mm, "end": v(-11.37, -11.41) * mm});
            skLineSegment(sketch, "E544", {"start": v(-11.56, -11.6) * mm, "end": v(-11.56, -11.22) * mm});
            skLineSegment(sketch, "E545", {"start": v(-12.76, -9) * mm, "end": v(-12.38, -9) * mm});
            skLineSegment(sketch, "E546", {"start": v(-12.57, -9.2) * mm, "end": v(-12.57, -8.8) * mm});
            skLineSegment(sketch, "E547", {"start": v(-20.26, -10.14) * mm, "end": v(-19.88, -10.14) * mm});
            skLineSegment(sketch, "E548", {"start": v(-20.07, -10.33) * mm, "end": v(-20.07, -9.95) * mm});
            skLineSegment(sketch, "E549", {"start": v(-20.51, -11.16) * mm, "end": v(-20.13, -11.16) * mm});
            skLineSegment(sketch, "E550", {"start": v(-20.32, -11.35) * mm, "end": v(-20.32, -10.97) * mm});
            skLineSegment(sketch, "E551", {"start": v(-19.5, -10.02) * mm, "end": v(-19.11, -10.02) * mm});
            skLineSegment(sketch, "E552", {"start": v(-19.3, -10.2) * mm, "end": v(-19.3, -9.83) * mm});
            skLineSegment(sketch, "E553", {"start": v(-21.27, -11.16) * mm, "end": v(-20.9, -11.16) * mm});
            skLineSegment(sketch, "E554", {"start": v(-21.08, -11.35) * mm, "end": v(-21.08, -10.97) * mm});
            skLineSegment(sketch, "E555", {"start": v(-20.9, -10.52) * mm, "end": v(-20.51, -10.52) * mm});
            skLineSegment(sketch, "E556", {"start": v(-20.7, -10.71) * mm, "end": v(-20.7, -10.33) * mm});
            skLineSegment(sketch, "E557", {"start": v(-21.53, -10.14) * mm, "end": v(-21.15, -10.14) * mm});
            skLineSegment(sketch, "E558", {"start": v(-21.34, -10.33) * mm, "end": v(-21.34, -9.95) * mm});
            skLineSegment(sketch, "E559", {"start": v(21.9, -7.35) * mm, "end": v(22.28, -7.35) * mm});
            skLineSegment(sketch, "E560", {"start": v(22.1, -7.54) * mm, "end": v(22.1, -7.16) * mm});
            skLineSegment(sketch, "E561", {"start": v(5.52, 17.92) * mm, "end": v(5.9, 17.92) * mm});
            skLineSegment(sketch, "E562", {"start": v(5.71, 17.73) * mm, "end": v(5.71, 18.11) * mm});
            skLineSegment(sketch, "E563", {"start": v(2.6, 14.75) * mm, "end": v(2.98, 14.75) * mm});
            skLineSegment(sketch, "E564", {"start": v(2.8, 14.56) * mm, "end": v(2.8, 14.94) * mm});
            skLineSegment(sketch, "E565", {"start": v(1.71, 2.68) * mm, "end": v(2.1, 2.68) * mm});
            skLineSegment(sketch, "E566", {"start": v(1.9, 2.5) * mm, "end": v(1.9, 2.87) * mm});
            skLineSegment(sketch, "E567", {"start": v(-0.7, 19.2) * mm, "end": v(-0.32, 19.2) * mm});
            skLineSegment(sketch, "E568", {"start": v(-0.5, 19) * mm, "end": v(-0.5, 19.38) * mm});
            skLineSegment(sketch, "E569", {"start": v(-0.57, 18.05) * mm, "end": v(-0.2, 18.05) * mm});
            skLineSegment(sketch, "E570", {"start": v(-0.38, 17.86) * mm, "end": v(-0.38, 18.24) * mm});
            skLineSegment(sketch, "E571", {"start": v(2.86, 18.56) * mm, "end": v(3.24, 18.56) * mm});
            skLineSegment(sketch, "E572", {"start": v(3.05, 18.37) * mm, "end": v(3.05, 18.75) * mm});
            skLineSegment(sketch, "E573", {"start": v(11.75, 3.57) * mm, "end": v(12.13, 3.57) * mm});
            skLineSegment(sketch, "E574", {"start": v(11.94, 3.38) * mm, "end": v(11.94, 3.76) * mm});
            skLineSegment(sketch, "E575", {"start": v(12.25, 2.68) * mm, "end": v(12.64, 2.68) * mm});
            skLineSegment(sketch, "E576", {"start": v(12.44, 2.5) * mm, "end": v(12.44, 2.87) * mm});
            skLineSegment(sketch, "E577", {"start": v(7.43, 1.29) * mm, "end": v(7.8, 1.29) * mm});
            skLineSegment(sketch, "E578", {"start": v(7.62, 1.1) * mm, "end": v(7.62, 1.48) * mm});
            skLineSegment(sketch, "E579", {"start": v(-1.08, -21.83) * mm, "end": v(-0.7, -21.83) * mm});
            skLineSegment(sketch, "E580", {"start": v(-0.9, -22.02) * mm, "end": v(-0.9, -21.64) * mm});
            skLineSegment(sketch, "E581", {"start": v(-22.86, 17.29) * mm, "end": v(-22.35, 17.29) * mm});
            skLineSegment(sketch, "E582", {"start": v(-22.6, 17.03) * mm, "end": v(-22.6, 17.54) * mm});
            skLineSegment(sketch, "E583", {"start": v(-8.57, 14.11) * mm, "end": v(-8.2, 14.11) * mm});
            skLineSegment(sketch, "E584", {"start": v(-8.38, 13.92) * mm, "end": v(-8.38, 14.3) * mm});
            skLineSegment(sketch, "E585", {"start": v(-5.27, -19.92) * mm, "end": v(-4.9, -19.92) * mm});
            skLineSegment(sketch, "E586", {"start": v(-5.08, -20.11) * mm, "end": v(-5.08, -19.73) * mm});
            skLineSegment(sketch, "E587", {"start": v(-3.75, -12.68) * mm, "end": v(-3.37, -12.68) * mm});
            skLineSegment(sketch, "E588", {"start": v(-3.56, -12.87) * mm, "end": v(-3.56, -12.5) * mm});
            skLineSegment(sketch, "E589", {"start": v(-3.11, -15.22) * mm, "end": v(-2.73, -15.22) * mm});
            skLineSegment(sketch, "E590", {"start": v(-2.92, -15.41) * mm, "end": v(-2.92, -15.03) * mm});
            skLineSegment(sketch, "E591", {"start": v(-21.9, -19.41) * mm, "end": v(-21.53, -19.41) * mm});
            skLineSegment(sketch, "E592", {"start": v(-21.72, -19.6) * mm, "end": v(-21.72, -19.22) * mm});
            skLineSegment(sketch, "E593", {"start": v(-9.72, -22.34) * mm, "end": v(-9.34, -22.34) * mm});
            skLineSegment(sketch, "E594", {"start": v(-9.53, -22.53) * mm, "end": v(-9.53, -22.14) * mm});
            skLineSegment(sketch, "E595", {"start": v(-11.5, -16.56) * mm, "end": v(-11.11, -16.56) * mm});
            skLineSegment(sketch, "E596", {"start": v(-11.3, -16.75) * mm, "end": v(-11.3, -16.37) * mm});
            skLineSegment(sketch, "E597", {"start": v(-24.45, -16.24) * mm, "end": v(-24.07, -16.24) * mm});
            skLineSegment(sketch, "E598", {"start": v(-24.26, -16.43) * mm, "end": v(-24.26, -16.05) * mm});
            skLineSegment(sketch, "E599", {"start": v(-18.86, -18.9) * mm, "end": v(-18.48, -18.9) * mm});
            skLineSegment(sketch, "E600", {"start": v(-18.67, -19.1) * mm, "end": v(-18.67, -18.72) * mm});
            skLineSegment(sketch, "E601", {"start": v(-19.9, -18.9) * mm, "end": v(-19.51, -18.9) * mm});
            skLineSegment(sketch, "E602", {"start": v(-19.7, -19.1) * mm, "end": v(-19.7, -18.72) * mm});
            skLineSegment(sketch, "E603", {"start": v(-29.02, -13.7) * mm, "end": v(-28.64, -13.7) * mm});
            skLineSegment(sketch, "E604", {"start": v(-28.83, -13.89) * mm, "end": v(-28.83, -13.5) * mm});
            skLineSegment(sketch, "E605", {"start": v(-17.2, -15.99) * mm, "end": v(-16.83, -15.99) * mm});
            skLineSegment(sketch, "E606", {"start": v(-17.02, -16.18) * mm, "end": v(-17.02, -15.8) * mm});
            skLineSegment(sketch, "E607", {"start": v(-15.3, -17.9) * mm, "end": v(-14.92, -17.9) * mm});
            skLineSegment(sketch, "E608", {"start": v(-15.11, -18.08) * mm, "end": v(-15.11, -17.7) * mm});
            skLineSegment(sketch, "E609", {"start": v(-17.2, -17.9) * mm, "end": v(-16.83, -17.9) * mm});
            skLineSegment(sketch, "E610", {"start": v(-17.02, -18.08) * mm, "end": v(-17.02, -17.7) * mm});
            skLineSegment(sketch, "E611", {"start": v(-11.75, -23.86) * mm, "end": v(-11.37, -23.86) * mm});
            skLineSegment(sketch, "E612", {"start": v(-11.56, -24.05) * mm, "end": v(-11.56, -23.67) * mm});
            skLineSegment(sketch, "E613", {"start": v(-6.92, -23.86) * mm, "end": v(-6.54, -23.86) * mm});
            skLineSegment(sketch, "E614", {"start": v(-6.73, -24.05) * mm, "end": v(-6.73, -23.67) * mm});
            skLineSegment(sketch, "E615", {"start": v(29.53, 11.7) * mm, "end": v(29.9, 11.7) * mm});
            skLineSegment(sketch, "E616", {"start": v(29.72, 11.51) * mm, "end": v(29.72, 11.9) * mm});
            skLineSegment(sketch, "E617", {"start": v(-1.08, 8.65) * mm, "end": v(-0.7, 8.65) * mm});
            skLineSegment(sketch, "E618", {"start": v(-0.9, 8.46) * mm, "end": v(-0.9, 8.84) * mm});
            skLineSegment(sketch, "E619", {"start": v(-4.26, 6.75) * mm, "end": v(-3.87, 6.75) * mm});
            skLineSegment(sketch, "E620", {"start": v(-4.07, 6.56) * mm, "end": v(-4.07, 6.94) * mm});
            skLineSegment(sketch, "E621", {"start": v(-3.75, 5.86) * mm, "end": v(-3.37, 5.86) * mm});
            skLineSegment(sketch, "E622", {"start": v(-3.56, 5.67) * mm, "end": v(-3.56, 6.05) * mm});
            skLineSegment(sketch, "E623", {"start": v(-3.87, 4.84) * mm, "end": v(-3.5, 4.84) * mm});
            skLineSegment(sketch, "E624", {"start": v(-3.68, 4.65) * mm, "end": v(-3.68, 5.03) * mm});
            skLineSegment(sketch, "E625", {"start": v(-4, 3.83) * mm, "end": v(-3.62, 3.83) * mm});
            skLineSegment(sketch, "E626", {"start": v(-3.81, 3.64) * mm, "end": v(-3.81, 4.02) * mm});
            skLineSegment(sketch, "E627", {"start": v(0.57, 1.54) * mm, "end": v(0.95, 1.54) * mm});
            skLineSegment(sketch, "E628", {"start": v(0.76, 1.35) * mm, "end": v(0.76, 1.73) * mm});
            skLineSegment(sketch, "E629", {"start": v(4.25, 3.45) * mm, "end": v(4.63, 3.45) * mm});
            skLineSegment(sketch, "E630", {"start": v(4.44, 3.26) * mm, "end": v(4.44, 3.64) * mm});
            skLineSegment(sketch, "E631", {"start": v(10.86, 1.03) * mm, "end": v(11.24, 1.03) * mm});
            skLineSegment(sketch, "E632", {"start": v(11.05, 0.84) * mm, "end": v(11.05, 1.22) * mm});
            skLineSegment(sketch, "E633", {"start": v(7.43, -2.14) * mm, "end": v(7.8, -2.14) * mm});
            skLineSegment(sketch, "E634", {"start": v(7.62, -2.33) * mm, "end": v(7.62, -1.95) * mm});
            skLineSegment(sketch, "E635", {"start": v(4.76, -2.14) * mm, "end": v(5.14, -2.14) * mm});
            skLineSegment(sketch, "E636", {"start": v(4.95, -2.33) * mm, "end": v(4.95, -1.95) * mm});
            skLineSegment(sketch, "E637", {"start": v(5.27, -3.16) * mm, "end": v(5.65, -3.16) * mm});
            skLineSegment(sketch, "E638", {"start": v(5.46, -3.35) * mm, "end": v(5.46, -2.97) * mm});
            skLineSegment(sketch, "E639", {"start": v(4.5, -9.89) * mm, "end": v(4.89, -9.89) * mm});
            skLineSegment(sketch, "E640", {"start": v(4.7, -10.08) * mm, "end": v(4.7, -9.7) * mm});
            skLineSegment(sketch, "E641", {"start": v(7.8, -3.67) * mm, "end": v(8.2, -3.67) * mm});
            skLineSegment(sketch, "E642", {"start": v(8, -3.86) * mm, "end": v(8, -3.48) * mm});
            skLineSegment(sketch, "E643", {"start": v(0.57, 0.52) * mm, "end": v(0.95, 0.52) * mm});
            skLineSegment(sketch, "E644", {"start": v(0.76, 0.33) * mm, "end": v(0.76, 0.72) * mm});
            skLineSegment(sketch, "E645", {"start": v(-8.7, 19.13) * mm, "end": v(-8.32, 19.13) * mm});
            skLineSegment(sketch, "E646", {"start": v(-8.51, 18.94) * mm, "end": v(-8.51, 19.32) * mm});
            skLineSegment(sketch, "E647", {"start": v(-7.68, 16.4) * mm, "end": v(-7.3, 16.4) * mm});
            skLineSegment(sketch, "E648", {"start": v(-7.5, 16.2) * mm, "end": v(-7.5, 16.6) * mm});
            skLineSegment(sketch, "E649", {"start": v(18.25, 12.84) * mm, "end": v(18.63, 12.84) * mm});
            skLineSegment(sketch, "E650", {"start": v(18.44, 12.65) * mm, "end": v(18.44, 13.03) * mm});
            skLineSegment(sketch, "E651", {"start": v(10.1, 16.78) * mm, "end": v(10.48, 16.78) * mm});
            skLineSegment(sketch, "E652", {"start": v(10.29, 16.6) * mm, "end": v(10.29, 16.97) * mm});
            skLineSegment(sketch, "E653", {"start": v(9.84, 12.97) * mm, "end": v(10.22, 12.97) * mm});
            skLineSegment(sketch, "E654", {"start": v(10.03, 12.78) * mm, "end": v(10.03, 13.16) * mm});
            skLineSegment(sketch, "E655", {"start": v(27.11, 2.43) * mm, "end": v(27.5, 2.43) * mm});
            skLineSegment(sketch, "E656", {"start": v(27.3, 2.24) * mm, "end": v(27.3, 2.62) * mm});
            skLineSegment(sketch, "E657", {"start": v(24.57, 2.43) * mm, "end": v(24.95, 2.43) * mm});
            skLineSegment(sketch, "E658", {"start": v(24.76, 2.24) * mm, "end": v(24.76, 2.62) * mm});
            skLineSegment(sketch, "E659", {"start": v(25.97, -0.36) * mm, "end": v(26.35, -0.36) * mm});
            skLineSegment(sketch, "E660", {"start": v(26.16, -0.55) * mm, "end": v(26.16, -0.17) * mm});
            skLineSegment(sketch, "E661", {"start": v(-10.86, 18.56) * mm, "end": v(-10.48, 18.56) * mm});
            skLineSegment(sketch, "E662", {"start": v(-10.67, 18.37) * mm, "end": v(-10.67, 18.75) * mm});
            skLineSegment(sketch, "E663", {"start": v(-7.76, -12.81) * mm, "end": v(-7.38, -12.81) * mm});
            skLineSegment(sketch, "E664", {"start": v(-7.57, -13) * mm, "end": v(-7.57, -12.62) * mm});
            skLineSegment(sketch, "E665", {"start": v(15.05, -10.45) * mm, "end": v(15.43, -10.45) * mm});
            skLineSegment(sketch, "E666", {"start": v(15.24, -10.64) * mm, "end": v(15.24, -10.26) * mm});
            skLineSegment(sketch, "E667", {"start": v(17.08, -25.26) * mm, "end": v(17.46, -25.26) * mm});
            skLineSegment(sketch, "E668", {"start": v(17.27, -25.45) * mm, "end": v(17.27, -25.07) * mm});
            skLineSegment(sketch, "E669", {"start": v(27.5, -21.83) * mm, "end": v(27.88, -21.83) * mm});
            skLineSegment(sketch, "E670", {"start": v(27.68, -22.02) * mm, "end": v(27.68, -21.64) * mm});
            skLineSegment(sketch, "E671", {"start": v(19.95, -10.52) * mm, "end": v(20.33, -10.52) * mm});
            skLineSegment(sketch, "E672", {"start": v(20.14, -10.71) * mm, "end": v(20.14, -10.33) * mm});
            skLineSegment(sketch, "E673", {"start": v(23.18, -22.84) * mm, "end": v(23.56, -22.84) * mm});
            skLineSegment(sketch, "E674", {"start": v(23.37, -23.03) * mm, "end": v(23.37, -22.65) * mm});
            skLineSegment(sketch, "E675", {"start": v(15.8, -22.84) * mm, "end": v(16.18, -22.84) * mm});
            skLineSegment(sketch, "E676", {"start": v(16, -23.03) * mm, "end": v(16, -22.65) * mm});
            skLineSegment(sketch, "E677", {"start": v(9.08, 0.52) * mm, "end": v(9.46, 0.52) * mm});
            skLineSegment(sketch, "E678", {"start": v(9.27, 0.33) * mm, "end": v(9.27, 0.72) * mm});
            skLineSegment(sketch, "E679", {"start": v(6.54, -0.87) * mm, "end": v(6.92, -0.87) * mm});
            skLineSegment(sketch, "E680", {"start": v(6.73, -1.06) * mm, "end": v(6.73, -0.68) * mm});
            skLineSegment(sketch, "E681", {"start": v(19.75, -11.8) * mm, "end": v(20.13, -11.8) * mm});
            skLineSegment(sketch, "E682", {"start": v(19.94, -11.98) * mm, "end": v(19.94, -11.6) * mm});
            skLineSegment(sketch, "E683", {"start": v(13.78, -1.13) * mm, "end": v(14.16, -1.13) * mm});
            skLineSegment(sketch, "E684", {"start": v(13.97, -1.32) * mm, "end": v(13.97, -0.94) * mm});
            skLineSegment(sketch, "E685", {"start": v(19.19, -9.89) * mm, "end": v(19.57, -9.89) * mm});
            skLineSegment(sketch, "E686", {"start": v(19.38, -10.08) * mm, "end": v(19.38, -9.7) * mm});
            skLineSegment(sketch, "E687", {"start": v(10.6, -6.2) * mm, "end": v(10.98, -6.2) * mm});
            skLineSegment(sketch, "E688", {"start": v(10.8, -6.4) * mm, "end": v(10.8, -6.02) * mm});
            skLineSegment(sketch, "E689", {"start": v(10.86, -9.89) * mm, "end": v(11.24, -9.89) * mm});
            skLineSegment(sketch, "E690", {"start": v(11.05, -10.08) * mm, "end": v(11.05, -9.7) * mm});
            skLineSegment(sketch, "E691", {"start": v(13.27, -7.86) * mm, "end": v(13.65, -7.86) * mm});
            skLineSegment(sketch, "E692", {"start": v(13.46, -8.05) * mm, "end": v(13.46, -7.67) * mm});
            skLineSegment(sketch, "E693", {"start": v(14.03, -10.4) * mm, "end": v(14.41, -10.4) * mm});
            skLineSegment(sketch, "E694", {"start": v(14.22, -10.59) * mm, "end": v(14.22, -10.2) * mm});
            skLineSegment(sketch, "E695", {"start": v(22.92, 1.99) * mm, "end": v(23.3, 1.99) * mm});
            skLineSegment(sketch, "E696", {"start": v(23.11, 1.8) * mm, "end": v(23.11, 2.18) * mm});
            skLineSegment(sketch, "E697", {"start": v(26.99, -6.08) * mm, "end": v(27.37, -6.08) * mm});
            skLineSegment(sketch, "E698", {"start": v(27.18, -6.27) * mm, "end": v(27.18, -5.89) * mm});
            skLineSegment(sketch, "E699", {"start": v(23.43, -7.48) * mm, "end": v(23.81, -7.48) * mm});
            skLineSegment(sketch, "E700", {"start": v(23.62, -7.67) * mm, "end": v(23.62, -7.29) * mm});
            skLineSegment(sketch, "E701", {"start": v(14.29, -7.35) * mm, "end": v(14.67, -7.35) * mm});
            skLineSegment(sketch, "E702", {"start": v(14.48, -7.54) * mm, "end": v(14.48, -7.16) * mm});
            skLineSegment(sketch, "E703", {"start": v(15.3, -7.34) * mm, "end": v(15.68, -7.34) * mm});
            skLineSegment(sketch, "E704", {"start": v(15.5, -7.53) * mm, "end": v(15.5, -7.15) * mm});
            skLineSegment(sketch, "E705", {"start": v(14.92, 1.54) * mm, "end": v(15.3, 1.54) * mm});
            skLineSegment(sketch, "E706", {"start": v(15.11, 1.35) * mm, "end": v(15.11, 1.73) * mm});
            skLineSegment(sketch, "E707", {"start": v(15.81, 1.03) * mm, "end": v(16.2, 1.03) * mm});
            skLineSegment(sketch, "E708", {"start": v(16, 0.84) * mm, "end": v(16, 1.22) * mm});
            skLineSegment(sketch, "E709", {"start": v(19.75, 2.05) * mm, "end": v(20.13, 2.05) * mm});
            skLineSegment(sketch, "E710", {"start": v(19.94, 1.86) * mm, "end": v(19.94, 2.24) * mm});
            skLineSegment(sketch, "E711", {"start": v(20.76, 0.52) * mm, "end": v(21.14, 0.52) * mm});
            skLineSegment(sketch, "E712", {"start": v(20.95, 0.33) * mm, "end": v(20.95, 0.72) * mm});
            skLineSegment(sketch, "E713", {"start": v(16.7, 1.54) * mm, "end": v(17.08, 1.54) * mm});
            skLineSegment(sketch, "E714", {"start": v(16.89, 1.35) * mm, "end": v(16.89, 1.73) * mm});
            skLineSegment(sketch, "E715", {"start": v(21.9, -0.75) * mm, "end": v(22.28, -0.75) * mm});
            skLineSegment(sketch, "E716", {"start": v(22.1, -0.94) * mm, "end": v(22.1, -0.55) * mm});
            skLineSegment(sketch, "E717", {"start": v(32.2, 5.73) * mm, "end": v(32.57, 5.73) * mm});
            skLineSegment(sketch, "E718", {"start": v(32.38, 5.54) * mm, "end": v(32.38, 5.92) * mm});
            skLineSegment(sketch, "E719", {"start": v(32.2, 0.02) * mm, "end": v(32.57, 0.02) * mm});
            skLineSegment(sketch, "E720", {"start": v(32.38, -0.17) * mm, "end": v(32.38, 0.2) * mm});
            skLineSegment(sketch, "E721", {"start": v(25.2, 0.4) * mm, "end": v(25.59, 0.4) * mm});
            skLineSegment(sketch, "E722", {"start": v(25.4, 0.2) * mm, "end": v(25.4, 0.59) * mm});
            skLineSegment(sketch, "E723", {"start": v(24.32, -4.3) * mm, "end": v(24.7, -4.3) * mm});
            skLineSegment(sketch, "E724", {"start": v(24.5, -4.5) * mm, "end": v(24.5, -4.11) * mm});
            skLineSegment(sketch, "E725", {"start": v(27.88, -8.75) * mm, "end": v(28.26, -8.75) * mm});
            skLineSegment(sketch, "E726", {"start": v(28.07, -8.94) * mm, "end": v(28.07, -8.56) * mm});
            skLineSegment(sketch, "E727", {"start": v(29.02, -8.75) * mm, "end": v(29.4, -8.75) * mm});
            skLineSegment(sketch, "E728", {"start": v(29.2, -8.94) * mm, "end": v(29.2, -8.56) * mm});
            skLineSegment(sketch, "E729", {"start": v(24.95, -11.54) * mm, "end": v(25.34, -11.54) * mm});
            skLineSegment(sketch, "E730", {"start": v(25.14, -11.73) * mm, "end": v(25.14, -11.35) * mm});
            skLineSegment(sketch, "E731", {"start": v(31.94, -10.78) * mm, "end": v(32.32, -10.78) * mm});
            skLineSegment(sketch, "E732", {"start": v(32.13, -10.97) * mm, "end": v(32.13, -10.59) * mm});
            skLineSegment(sketch, "E733", {"start": v(24.32, -10.02) * mm, "end": v(24.7, -10.02) * mm});
            skLineSegment(sketch, "E734", {"start": v(24.5, -10.2) * mm, "end": v(24.5, -9.83) * mm});
            skLineSegment(sketch, "E735", {"start": v(27.24, 0.02) * mm, "end": v(27.62, 0.02) * mm});
            skLineSegment(sketch, "E736", {"start": v(27.43, -0.17) * mm, "end": v(27.43, 0.2) * mm});
            skLineSegment(sketch, "E737", {"start": v(29.9, -10.78) * mm, "end": v(30.29, -10.78) * mm});
            skLineSegment(sketch, "E738", {"start": v(30.1, -10.97) * mm, "end": v(30.1, -10.59) * mm});
            skLineSegment(sketch, "E739", {"start": v(-21.15, -19.41) * mm, "end": v(-20.77, -19.41) * mm});
            skLineSegment(sketch, "E740", {"start": v(-20.96, -19.6) * mm, "end": v(-20.96, -19.22) * mm});
            skLineSegment(sketch, "E741", {"start": v(-3.11, -15.99) * mm, "end": v(-2.73, -15.99) * mm});
            skLineSegment(sketch, "E742", {"start": v(-2.92, -16.18) * mm, "end": v(-2.92, -15.8) * mm});
            skLineSegment(sketch, "E743", {"start": v(-7.94, 23.9) * mm, "end": v(-7.56, 23.9) * mm});
            skLineSegment(sketch, "E744", {"start": v(-7.75, 23.7) * mm, "end": v(-7.75, 24.08) * mm});
            skLineSegment(sketch, "E745", {"start": v(-12, 22.75) * mm, "end": v(-11.62, 22.75) * mm});
            skLineSegment(sketch, "E746", {"start": v(-11.81, 22.56) * mm, "end": v(-11.81, 22.94) * mm});
            skLineSegment(sketch, "E747", {"start": v(-18.1, 23.9) * mm, "end": v(-17.72, 23.9) * mm});
            skLineSegment(sketch, "E748", {"start": v(-17.9, 23.7) * mm, "end": v(-17.9, 24.08) * mm});
            skLineSegment(sketch, "E749", {"start": v(-14.8, 22.62) * mm, "end": v(-14.42, 22.62) * mm});
            skLineSegment(sketch, "E750", {"start": v(-14.6, 22.43) * mm, "end": v(-14.6, 22.81) * mm});
            skLineSegment(sketch, "E751", {"start": v(-2.22, -0.36) * mm, "end": v(-1.84, -0.36) * mm});
            skLineSegment(sketch, "E752", {"start": v(-2.03, -0.55) * mm, "end": v(-2.03, -0.17) * mm});
            skLineSegment(sketch, "E753", {"start": v(-29.02, -6.33) * mm, "end": v(-28.64, -6.33) * mm});
            skLineSegment(sketch, "E754", {"start": v(-28.83, -6.52) * mm, "end": v(-28.83, -6.14) * mm});
            skLineSegment(sketch, "E755", {"start": v(-24.45, -5.83) * mm, "end": v(-24.07, -5.83) * mm});
            skLineSegment(sketch, "E756", {"start": v(-24.26, -6.02) * mm, "end": v(-24.26, -5.63) * mm});
            skLineSegment(sketch, "E757", {"start": v(-24.45, -4.3) * mm, "end": v(-24.07, -4.3) * mm});
            skLineSegment(sketch, "E758", {"start": v(-24.26, -4.5) * mm, "end": v(-24.26, -4.11) * mm});
            skLineSegment(sketch, "E759", {"start": v(-14.42, -22.34) * mm, "end": v(-14.03, -22.34) * mm});
            skLineSegment(sketch, "E760", {"start": v(-14.23, -22.53) * mm, "end": v(-14.23, -22.14) * mm});
            skLineSegment(sketch, "E761", {"start": v(-14.42, -23.86) * mm, "end": v(-14.03, -23.86) * mm});
            skLineSegment(sketch, "E762", {"start": v(-14.23, -24.05) * mm, "end": v(-14.23, -23.67) * mm});
            skLineSegment(sketch, "E763", {"start": v(-22.8, -17.9) * mm, "end": v(-22.42, -17.9) * mm});
            skLineSegment(sketch, "E764", {"start": v(-22.6, -18.08) * mm, "end": v(-22.6, -17.7) * mm});
            skLineSegment(sketch, "E765", {"start": v(-29.02, -17.9) * mm, "end": v(-28.64, -17.9) * mm});
            skLineSegment(sketch, "E766", {"start": v(-28.83, -18.08) * mm, "end": v(-28.83, -17.7) * mm});
            skLineSegment(sketch, "E767", {"start": v(-24.45, -11.54) * mm, "end": v(-24.07, -11.54) * mm});
            skLineSegment(sketch, "E768", {"start": v(-24.26, -11.73) * mm, "end": v(-24.26, -11.35) * mm});
            skLineSegment(sketch, "E769", {"start": v(-1.84, -24.37) * mm, "end": v(-1.46, -24.37) * mm});
            skLineSegment(sketch, "E770", {"start": v(-1.65, -24.56) * mm, "end": v(-1.65, -24.18) * mm});
            skLineSegment(sketch, "E771", {"start": v(-1.84, -19.03) * mm, "end": v(-1.46, -19.03) * mm});
            skLineSegment(sketch, "E772", {"start": v(-1.65, -19.22) * mm, "end": v(-1.65, -18.84) * mm});
            skLineSegment(sketch, "E773", {"start": v(-1.08, -19.03) * mm, "end": v(-0.7, -19.03) * mm});
            skLineSegment(sketch, "E774", {"start": v(-0.9, -19.22) * mm, "end": v(-0.9, -18.84) * mm});
            skLineSegment(sketch, "E775", {"start": v(6.41, -19.8) * mm, "end": v(6.8, -19.8) * mm});
            skLineSegment(sketch, "E776", {"start": v(6.6, -19.99) * mm, "end": v(6.6, -19.6) * mm});
            skLineSegment(sketch, "E777", {"start": v(10.6, -19.8) * mm, "end": v(10.98, -19.8) * mm});
            skLineSegment(sketch, "E778", {"start": v(10.8, -19.99) * mm, "end": v(10.8, -19.6) * mm});
            skLineSegment(sketch, "E779", {"start": v(10.1, -22.72) * mm, "end": v(10.48, -22.72) * mm});
            skLineSegment(sketch, "E780", {"start": v(10.29, -22.9) * mm, "end": v(10.29, -22.53) * mm});
            skLineSegment(sketch, "E781", {"start": v(8.44, 18.43) * mm, "end": v(8.83, 18.43) * mm});
            skLineSegment(sketch, "E782", {"start": v(8.63, 18.24) * mm, "end": v(8.63, 18.62) * mm});
            skLineSegment(sketch, "E783", {"start": v(28.9, 18.69) * mm, "end": v(29.27, 18.69) * mm});
            skLineSegment(sketch, "E784", {"start": v(29.08, 18.5) * mm, "end": v(29.08, 18.88) * mm});
            skLineSegment(sketch, "E785", {"start": v(25.87, 12.84) * mm, "end": v(26.25, 12.84) * mm});
            skLineSegment(sketch, "E786", {"start": v(26.06, 12.65) * mm, "end": v(26.06, 13.03) * mm});
            skLineSegment(sketch, "E787", {"start": v(30.67, 11.7) * mm, "end": v(31.05, 11.7) * mm});
            skLineSegment(sketch, "E788", {"start": v(30.86, 11.51) * mm, "end": v(30.86, 11.9) * mm});
            skLineSegment(sketch, "E789", {"start": v(-1.65, 14.24) * mm, "end": v(-1.14, 14.24) * mm});
            skLineSegment(sketch, "E790", {"start": v(-1.4, 13.99) * mm, "end": v(-1.4, 14.5) * mm});
            skLineSegment(sketch, "E791", {"start": v(11.11, 20.08) * mm, "end": v(11.5, 20.08) * mm});
            skLineSegment(sketch, "E792", {"start": v(11.3, 19.9) * mm, "end": v(11.3, 20.27) * mm});
            skLineSegment(sketch, "E793", {"start": v(2.6, 12.72) * mm, "end": v(2.98, 12.72) * mm});
            skLineSegment(sketch, "E794", {"start": v(2.8, 12.53) * mm, "end": v(2.8, 12.9) * mm});
            skLineSegment(sketch, "E795", {"start": v(-14.16, 18.94) * mm, "end": v(-13.78, 18.94) * mm});
            skLineSegment(sketch, "E796", {"start": v(-13.97, 18.75) * mm, "end": v(-13.97, 19.13) * mm});
            skLineSegment(sketch, "E797", {"start": v(-25.34, 15.64) * mm, "end": v(-24.96, 15.64) * mm});
            skLineSegment(sketch, "E798", {"start": v(-25.15, 15.45) * mm, "end": v(-25.15, 15.83) * mm});
            skLineSegment(sketch, "E799", {"start": v(-24.58, 15.64) * mm, "end": v(-24.2, 15.64) * mm});
            skLineSegment(sketch, "E800", {"start": v(-24.39, 15.45) * mm, "end": v(-24.39, 15.83) * mm});
            skLineSegment(sketch, "E801", {"start": v(-23.81, 15.64) * mm, "end": v(-23.43, 15.64) * mm});
            skLineSegment(sketch, "E802", {"start": v(-23.62, 15.45) * mm, "end": v(-23.62, 15.83) * mm});
            skLineSegment(sketch, "E803", {"start": v(-23.43, 24.4) * mm, "end": v(-23.05, 24.4) * mm});
            skLineSegment(sketch, "E804", {"start": v(-23.24, 24.21) * mm, "end": v(-23.24, 24.6) * mm});
            skLineSegment(sketch, "E805", {"start": v(-22.92, 26.3) * mm, "end": v(-22.54, 26.3) * mm});
            skLineSegment(sketch, "E806", {"start": v(-22.73, 26.12) * mm, "end": v(-22.73, 26.5) * mm});
            skLineSegment(sketch, "E807", {"start": v(-23.43, 28.46) * mm, "end": v(-23.05, 28.46) * mm});
            skLineSegment(sketch, "E808", {"start": v(-23.24, 28.27) * mm, "end": v(-23.24, 28.66) * mm});
            skLineSegment(sketch, "E809", {"start": v(-22.04, 18.3) * mm, "end": v(-21.65, 18.3) * mm});
            skLineSegment(sketch, "E810", {"start": v(-21.85, 18.11) * mm, "end": v(-21.85, 18.5) * mm});
            skLineSegment(sketch, "E811", {"start": v(-21.27, 13.73) * mm, "end": v(-20.9, 13.73) * mm});
            skLineSegment(sketch, "E812", {"start": v(-21.08, 13.54) * mm, "end": v(-21.08, 13.92) * mm});
            skLineSegment(sketch, "E813", {"start": v(-20, 17.16) * mm, "end": v(-19.62, 17.16) * mm});
            skLineSegment(sketch, "E814", {"start": v(-19.81, 16.97) * mm, "end": v(-19.81, 17.35) * mm});
            skLineSegment(sketch, "E815", {"start": v(-14.42, 9.29) * mm, "end": v(-14.03, 9.29) * mm});
            skLineSegment(sketch, "E816", {"start": v(-14.23, 9.1) * mm, "end": v(-14.23, 9.48) * mm});
            skLineSegment(sketch, "E817", {"start": v(-14.42, 8.4) * mm, "end": v(-14.03, 8.4) * mm});
            skLineSegment(sketch, "E818", {"start": v(-14.23, 8.2) * mm, "end": v(-14.23, 8.59) * mm});
            skLineSegment(sketch, "E819", {"start": v(-24.45, -5.06) * mm, "end": v(-24.07, -5.06) * mm});
            skLineSegment(sketch, "E820", {"start": v(-24.26, -5.25) * mm, "end": v(-24.26, -4.87) * mm});
            skLineSegment(sketch, "E821", {"start": v(-22.99, -16.24) * mm, "end": v(-22.48, -16.24) * mm});
            skLineSegment(sketch, "E822", {"start": v(-22.73, -16.5) * mm, "end": v(-22.73, -15.99) * mm});
            skLineSegment(sketch, "E823", {"start": v(-19.05, -11.03) * mm, "end": v(-18.54, -11.03) * mm});
            skLineSegment(sketch, "E824", {"start": v(-18.8, -11.29) * mm, "end": v(-18.8, -10.78) * mm});
            skLineSegment(sketch, "E825", {"start": v(-15.94, -16.11) * mm, "end": v(-15.56, -16.11) * mm});
            skLineSegment(sketch, "E826", {"start": v(-15.75, -16.3) * mm, "end": v(-15.75, -15.92) * mm});
            skLineSegment(sketch, "E827", {"start": v(-14.29, -4.05) * mm, "end": v(-13.9, -4.05) * mm});
            skLineSegment(sketch, "E828", {"start": v(-14.1, -4.24) * mm, "end": v(-14.1, -3.86) * mm});
            skLineSegment(sketch, "E829", {"start": v(-15.43, -4.68) * mm, "end": v(-15.05, -4.68) * mm});
            skLineSegment(sketch, "E830", {"start": v(-15.24, -4.87) * mm, "end": v(-15.24, -4.5) * mm});
            skLineSegment(sketch, "E831", {"start": v(-14.67, -4.68) * mm, "end": v(-14.29, -4.68) * mm});
            skLineSegment(sketch, "E832", {"start": v(-14.48, -4.87) * mm, "end": v(-14.48, -4.5) * mm});
            skLineSegment(sketch, "E833", {"start": v(-13.9, -4.68) * mm, "end": v(-13.53, -4.68) * mm});
            skLineSegment(sketch, "E834", {"start": v(-13.72, -4.87) * mm, "end": v(-13.72, -4.5) * mm});
            skLineSegment(sketch, "E835", {"start": v(-15.05, -4.05) * mm, "end": v(-14.67, -4.05) * mm});
            skLineSegment(sketch, "E836", {"start": v(-14.86, -4.24) * mm, "end": v(-14.86, -3.86) * mm});
            skLineSegment(sketch, "E837", {"start": v(-16.2, -3.41) * mm, "end": v(-15.81, -3.41) * mm});
            skLineSegment(sketch, "E838", {"start": v(-16, -3.6) * mm, "end": v(-16, -3.22) * mm});
            skLineSegment(sketch, "E839", {"start": v(-18.48, -3.41) * mm, "end": v(-18.1, -3.41) * mm});
            skLineSegment(sketch, "E840", {"start": v(-18.29, -3.6) * mm, "end": v(-18.29, -3.22) * mm});
            skLineSegment(sketch, "E841", {"start": v(-17.34, -3.41) * mm, "end": v(-16.96, -3.41) * mm});
            skLineSegment(sketch, "E842", {"start": v(-17.15, -3.6) * mm, "end": v(-17.15, -3.22) * mm});
            skLineSegment(sketch, "E843", {"start": v(-14.42, -1.25) * mm, "end": v(-14.03, -1.25) * mm});
            skLineSegment(sketch, "E844", {"start": v(-14.23, -1.44) * mm, "end": v(-14.23, -1.06) * mm});
            skLineSegment(sketch, "E845", {"start": v(-10.6, -12.81) * mm, "end": v(-10.22, -12.81) * mm});
            skLineSegment(sketch, "E846", {"start": v(-10.42, -13) * mm, "end": v(-10.42, -12.62) * mm});
            skLineSegment(sketch, "E847", {"start": v(-15.3, -13.32) * mm, "end": v(-14.92, -13.32) * mm});
            skLineSegment(sketch, "E848", {"start": v(-15.11, -13.5) * mm, "end": v(-15.11, -13.13) * mm});
            skLineSegment(sketch, "E849", {"start": v(-22.8, -4.8) * mm, "end": v(-22.41, -4.8) * mm});
            skLineSegment(sketch, "E850", {"start": v(-22.6, -5) * mm, "end": v(-22.6, -4.62) * mm});
            skLineSegment(sketch, "E851", {"start": v(-22.29, -5.44) * mm, "end": v(-21.9, -5.44) * mm});
            skLineSegment(sketch, "E852", {"start": v(-22.1, -5.63) * mm, "end": v(-22.1, -5.25) * mm});
            skLineSegment(sketch, "E853", {"start": v(-22.29, -4.17) * mm, "end": v(-21.9, -4.17) * mm});
            skLineSegment(sketch, "E854", {"start": v(-22.1, -4.36) * mm, "end": v(-22.1, -3.98) * mm});
            skLineSegment(sketch, "E855", {"start": v(-13.65, -1.13) * mm, "end": v(-13.27, -1.13) * mm});
            skLineSegment(sketch, "E856", {"start": v(-13.46, -1.32) * mm, "end": v(-13.46, -0.94) * mm});
            skLineSegment(sketch, "E857", {"start": v(-14.42, -0.5) * mm, "end": v(-14.03, -0.5) * mm});
            skLineSegment(sketch, "E858", {"start": v(-14.23, -0.68) * mm, "end": v(-14.23, -0.3) * mm});
            skLineSegment(sketch, "E859", {"start": v(-12.9, -1) * mm, "end": v(-12.51, -1) * mm});
            skLineSegment(sketch, "E860", {"start": v(-12.7, -1.19) * mm, "end": v(-12.7, -0.8) * mm});
            skLineSegment(sketch, "E861", {"start": v(-14.42, 0.27) * mm, "end": v(-14.03, 0.27) * mm});
            skLineSegment(sketch, "E862", {"start": v(-14.23, 0.08) * mm, "end": v(-14.23, 0.46) * mm});
            skLineSegment(sketch, "E863", {"start": v(-16.2, 6.11) * mm, "end": v(-15.81, 6.11) * mm});
            skLineSegment(sketch, "E864", {"start": v(-16, 5.92) * mm, "end": v(-16, 6.3) * mm});
            skLineSegment(sketch, "E865", {"start": v(-11.62, -12.81) * mm, "end": v(-11.24, -12.81) * mm});
            skLineSegment(sketch, "E866", {"start": v(-11.43, -13) * mm, "end": v(-11.43, -12.62) * mm});
            skLineSegment(sketch, "E867", {"start": v(-13.65, -0.36) * mm, "end": v(-13.27, -0.36) * mm});
            skLineSegment(sketch, "E868", {"start": v(-13.46, -0.55) * mm, "end": v(-13.46, -0.17) * mm});
            skLineSegment(sketch, "E869", {"start": v(-24.45, -13.7) * mm, "end": v(-24.07, -13.7) * mm});
            skLineSegment(sketch, "E870", {"start": v(-24.26, -13.89) * mm, "end": v(-24.26, -13.5) * mm});
            skLineSegment(sketch, "E871", {"start": v(-9.46, -15.99) * mm, "end": v(-9.08, -15.99) * mm});
            skLineSegment(sketch, "E872", {"start": v(-9.27, -16.18) * mm, "end": v(-9.27, -15.8) * mm});
            skLineSegment(sketch, "E873", {"start": v(-26.99, -16.24) * mm, "end": v(-26.6, -16.24) * mm});
            skLineSegment(sketch, "E874", {"start": v(-26.8, -16.43) * mm, "end": v(-26.8, -16.05) * mm});
            skLineSegment(sketch, "E875", {"start": v(-6.29, -14.46) * mm, "end": v(-5.9, -14.46) * mm});
            skLineSegment(sketch, "E876", {"start": v(-6.1, -14.65) * mm, "end": v(-6.1, -14.27) * mm});
            skLineSegment(sketch, "E877", {"start": v(-5.89, -13.66) * mm, "end": v(-5.5, -13.66) * mm});
            skLineSegment(sketch, "E878", {"start": v(-5.7, -13.85) * mm, "end": v(-5.7, -13.47) * mm});
            skLineSegment(sketch, "E879", {"start": v(-5.89, -15.26) * mm, "end": v(-5.5, -15.26) * mm});
            skLineSegment(sketch, "E880", {"start": v(-5.7, -15.45) * mm, "end": v(-5.7, -15.07) * mm});
            skLineSegment(sketch, "E881", {"start": v(-6.69, -15.26) * mm, "end": v(-6.3, -15.26) * mm});
            skLineSegment(sketch, "E882", {"start": v(-6.5, -15.45) * mm, "end": v(-6.5, -15.07) * mm});
            skLineSegment(sketch, "E883", {"start": v(-6.69, -13.66) * mm, "end": v(-6.3, -13.66) * mm});
            skLineSegment(sketch, "E884", {"start": v(-6.5, -13.85) * mm, "end": v(-6.5, -13.47) * mm});
            skLineSegment(sketch, "E885", {"start": v(-20.77, 4) * mm, "end": v(-20.38, 4) * mm});
            skLineSegment(sketch, "E886", {"start": v(-20.58, 3.81) * mm, "end": v(-20.58, 4.2) * mm});
            skLineSegment(sketch, "E887", {"start": v(-21.62, 4.45) * mm, "end": v(-21.24, 4.45) * mm});
            skLineSegment(sketch, "E888", {"start": v(-21.43, 4.26) * mm, "end": v(-21.43, 4.64) * mm});
            skLineSegment(sketch, "E889", {"start": v(-21.62, 3.55) * mm, "end": v(-21.24, 3.55) * mm});
            skLineSegment(sketch, "E890", {"start": v(-21.43, 3.36) * mm, "end": v(-21.43, 3.75) * mm});
            skLineSegment(sketch, "E891", {"start": v(-19.91, 3.55) * mm, "end": v(-19.53, 3.55) * mm});
            skLineSegment(sketch, "E892", {"start": v(-19.72, 3.36) * mm, "end": v(-19.72, 3.75) * mm});
            skLineSegment(sketch, "E893", {"start": v(-19.91, 4.45) * mm, "end": v(-19.53, 4.45) * mm});
            skLineSegment(sketch, "E894", {"start": v(-19.72, 4.26) * mm, "end": v(-19.72, 4.64) * mm});
            skLineSegment(sketch, "E895", {"start": v(20.48, -3.92) * mm, "end": v(20.86, -3.92) * mm});
            skLineSegment(sketch, "E896", {"start": v(20.67, -4.11) * mm, "end": v(20.67, -3.73) * mm});
            skLineSegment(sketch, "E897", {"start": v(20.48, -1.92) * mm, "end": v(20.86, -1.92) * mm});
            skLineSegment(sketch, "E898", {"start": v(20.67, -2.11) * mm, "end": v(20.67, -1.73) * mm});
            skLineSegment(sketch, "E899", {"start": v(20.48, -5.92) * mm, "end": v(20.86, -5.92) * mm});
            skLineSegment(sketch, "E900", {"start": v(20.67, -6.1) * mm, "end": v(20.67, -5.73) * mm});
            skLineSegment(sketch, "E901", {"start": v(16.48, -1.92) * mm, "end": v(16.86, -1.92) * mm});
            skLineSegment(sketch, "E902", {"start": v(16.67, -2.11) * mm, "end": v(16.67, -1.73) * mm});
            skLineSegment(sketch, "E903", {"start": v(16.48, -3.92) * mm, "end": v(16.86, -3.92) * mm});
            skLineSegment(sketch, "E904", {"start": v(16.67, -4.11) * mm, "end": v(16.67, -3.73) * mm});
            skLineSegment(sketch, "E905", {"start": v(16.48, -5.92) * mm, "end": v(16.86, -5.92) * mm});
            skLineSegment(sketch, "E906", {"start": v(16.67, -6.1) * mm, "end": v(16.67, -5.73) * mm});
            skLineSegment(sketch, "E907", {"start": v(-20.77, 9.54) * mm, "end": v(-20.38, 9.54) * mm});
            skLineSegment(sketch, "E908", {"start": v(-20.58, 9.35) * mm, "end": v(-20.58, 9.73) * mm});
            skLineSegment(sketch, "E909", {"start": v(-21.62, 10) * mm, "end": v(-21.24, 10) * mm});
            skLineSegment(sketch, "E910", {"start": v(-21.43, 9.8) * mm, "end": v(-21.43, 10.18) * mm});
            skLineSegment(sketch, "E911", {"start": v(-21.62, 9.1) * mm, "end": v(-21.24, 9.1) * mm});
            skLineSegment(sketch, "E912", {"start": v(-21.43, 8.9) * mm, "end": v(-21.43, 9.28) * mm});
            skLineSegment(sketch, "E913", {"start": v(-19.91, 9.1) * mm, "end": v(-19.53, 9.1) * mm});
            skLineSegment(sketch, "E914", {"start": v(-19.72, 8.9) * mm, "end": v(-19.72, 9.28) * mm});
            skLineSegment(sketch, "E915", {"start": v(-19.91, 10) * mm, "end": v(-19.53, 10) * mm});
            skLineSegment(sketch, "E916", {"start": v(-19.72, 9.8) * mm, "end": v(-19.72, 10.18) * mm});
            skLineSegment(sketch, "E917", {"start": v(-27.1, -26.27) * mm, "end": v(-24.64, -26.27) * mm});
            skCircle(sketch, "E918", {"center": v(-26.6, 26.23) * mm, "radius": 1.37 * mm});
            skCircle(sketch, "E919", {"center": v(31.4, 26.23) * mm, "radius": 1.38 * mm});
            skCircle(sketch, "E920", {"center": v(31.4, -22.77) * mm, "radius": 1.37 * mm});
            skCircle(sketch, "E921", {"center": v(-26.6, -22.77) * mm, "radius": 1.37 * mm});
            skSolve(sketch);
        }
        {
            var Q0;
            Q0 = qSketchRegion(id + "F0", true);
            extrude(context, id + "F1", {"entities" : qUnion([Q0]), "depth" : 1.6 * mm, "offsetDistance" : 25 * mm});
        }
        {
            var Q0;
            Q0=makeQuery(id+"F1.opExtrude","CAP_FACE",FACE,{"disambiguationData":[OSD([sQuery(id+"F0.wireOp",EDGE,"E0"),sQuery(id+"F0.wireOp",EDGE,"E1"),sQuery(id+"F0.wireOp",EDGE,"E2"),sQuery(id+"F0.wireOp",EDGE,"E3"),sQuery(id+"F0.wireOp",EDGE,"E4"),sQuery(id+"F0.wireOp",EDGE,"E5"),sQuery(id+"F0.wireOp",EDGE,"E6"),sQuery(id+"F0.wireOp",EDGE,"E7"),sQuery(id+"F0.wireOp",EDGE,"E8"),sQuery(id+"F0.wireOp",EDGE,"E9"),sQuery(id+"F0.wireOp",EDGE,"E10"),sQuery(id+"F0.wireOp",EDGE,"E917"),sQuery(id+"F0.wireOp",EDGE,"E918"),sQuery(id+"F0.wireOp",EDGE,"E919"),sQuery(id+"F0.wireOp",EDGE,"E920"),sQuery(id+"F0.wireOp",EDGE,"E921")])],"isStart":false});
            var sketch = newSketch(context, id + "F2", { "sketchPlane" : qUnion([Q0])});
            skCircle(sketch, "E922", {"center": v(-18.9, -2.74) * mm, "radius": 3.3 * mm});
            skCircle(sketch, "E923", {"center": v(-10.61, -2.4) * mm, "radius": 3.3 * mm});
            skSolve(sketch);
        }
        {
            var Q0;
            Q0=makeQuery(id+"F2.imprint","IMPRINT",FACE,{"disambiguationData":[TD([[makeQuery(id+"F2.imprint","IMPRINT",EDGE,{"derivedFrom":sQuery(id+"F2.wireOp",EDGE,"E922")}),1.0]])]});
            var Q1;
            Q1=makeQuery(id+"F2.imprint","IMPRINT",FACE,{"disambiguationData":[TD([[makeQuery(id+"F2.imprint","IMPRINT",EDGE,{"derivedFrom":sQuery(id+"F2.wireOp",EDGE,"E923")}),1.0]])]});
            extrude(context, id + "F3", {"entities" : qUnion([Q0, Q1]), "operationType" : NewBodyOperationType.ADD, "depth" : 8 * mm, "offsetDistance" : 25 * mm});
        }
    });
